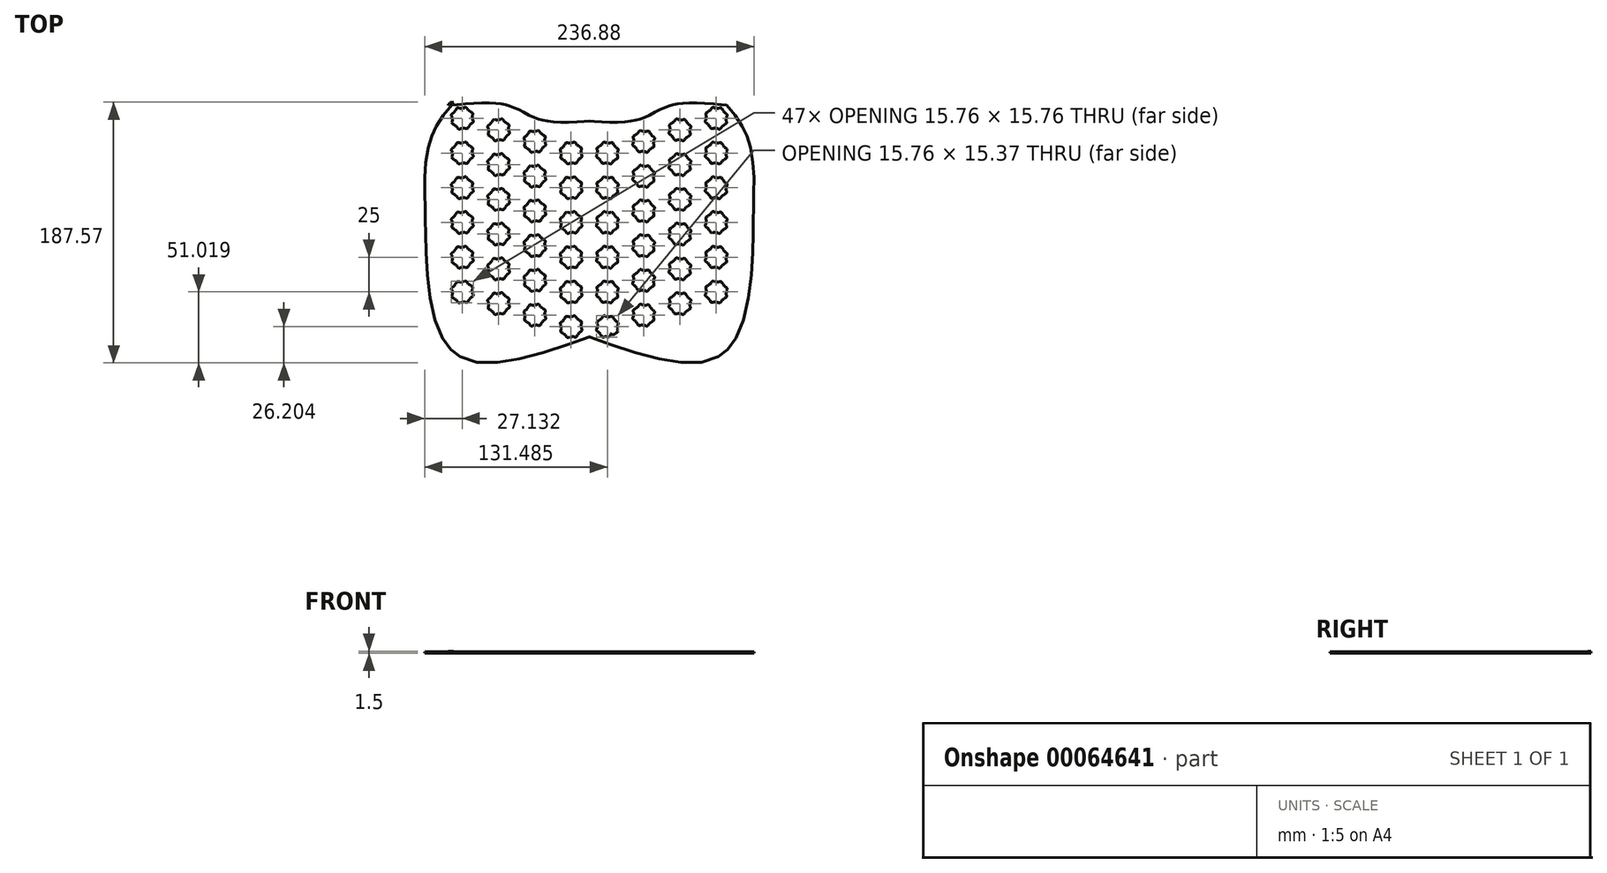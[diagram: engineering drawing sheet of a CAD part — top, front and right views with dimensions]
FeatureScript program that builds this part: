
annotation { "Feature Type Name" : "Feature", "Feature Type Description" : "" }
export const myFeature = defineFeature(function(context is Context, id is Id, definition is map)
    precondition{}
    {
        {
            var Q0;
            Q0=qCreatedBy(makeId("Top.planeOp"),FACE);
            var sketch = newSketch(context, id + "F0", { "sketchPlane" : qUnion([Q0])});
            skLineSegment(sketch, "E0", {"start": v(-116.5, 0) * mm, "end": v(139.03, 0) * mm, "construction": true});
            skLineSegment(sketch, "E1.0", {"start": v(-116.5, -90) * mm, "end": v(139.03, -90) * mm, "construction": true});
            skLineSegment(sketch, "E2.0", {"start": v(-116.5, 90) * mm, "end": v(139.03, 90) * mm, "construction": true});
            skLineSegment(sketch, "E3", {"start": v(0, 90) * mm, "end": v(0, -92.69) * mm, "construction": true});
            skLineSegment(sketch, "E4.0", {"start": v(-100, 90) * mm, "end": v(-100, -92.69) * mm, "construction": true});
            skLineSegment(sketch, "E5.0", {"start": v(-120, 90) * mm, "end": v(-120, -92.69) * mm, "construction": true});
            skLineSegment(sketch, "E6.0", {"start": v(120, 90) * mm, "end": v(120, -92.69) * mm, "construction": true});
            skLineSegment(sketch, "E7.0", {"start": v(100, 90) * mm, "end": v(100, -92.69) * mm, "construction": true});
            skFitSpline(sketch, "E8", {"points": [v(-100, 90) * mm, v(-114.02, 69.47) * mm, v(-120, 43.4) * mm, v(-120, 8.31) * mm, v(-100, -90) * mm, v(0, -80.79) * mm], "startDerivative": vector(-114.58, -138.92) * mm, "endDerivative": vector(433.2, 151.03) * mm});
            skFitSpline(sketch, "E9", {"points": [v(0, 78.79) * mm, v(-34.86, 79.72) * mm, v(-58.45, 90) * mm, v(-100, 90) * mm], "startDerivative": vector(-110.99, -8.68) * mm, "endDerivative": vector(-123.02, -12.63) * mm});
            skArc(sketch, "E10.filletArc", {"start": v(-97.54, 90.25) * mm, "mid": v(-99.77, 89.57) * mm, "end": v(-101.57, 88.09) * mm});
            skFitSpline(sketch, "E11.MirrorCS", {"points": [v(0, 78.79) * mm, v(34.86, 79.72) * mm, v(58.45, 90) * mm, v(100, 90) * mm], "startDerivative": vector(110.99, -8.68) * mm, "endDerivative": vector(123.02, -12.63) * mm});
            skFitSpline(sketch, "E12.MirrorCS", {"points": [v(100, 90) * mm, v(114.02, 69.47) * mm, v(120, 43.4) * mm, v(120, 8.31) * mm, v(100, -90) * mm, v(0, -80.79) * mm], "startDerivative": vector(114.58, -138.92) * mm, "endDerivative": vector(-433.2, 151.03) * mm});
            skArc(sketch, "E13.MirrorCS", {"start": v(97.54, 90.25) * mm, "mid": v(99.77, 89.57) * mm, "end": v(101.57, 88.09) * mm});
            skFitSpline(sketch, "E14.0", {"points": [v(0.16, 76.8) * mm, v(-2.16, 76.61) * mm, v(-6.8, 76.25) * mm, v(-13.69, 75.85) * mm, v(-20.42, 75.74) * mm, v(-25.82, 76.02) * mm, v(-29.97, 76.55) * mm, v(-32.48, 77.03) * mm, v(-34.44, 77.51) * mm, v(-36.35, 78.06) * mm, v(-38.65, 78.88) * mm, v(-41.26, 80) * mm, v(-44.61, 81.61) * mm, v(-47.82, 83.32) * mm, v(-51.02, 84.95) * mm, v(-53.45, 86.09) * mm, v(-55.94, 87.11) * mm, v(-58.1, 87.84) * mm, v(-59.9, 88.32) * mm, v(-61.76, 88.75) * mm, v(-64.2, 89.18) * mm, v(-67.3, 89.53) * mm, v(-71.61, 89.8) * mm, v(-77.33, 89.83) * mm, v(-84.6, 89.45) * mm, v(-92.12, 88.8) * mm, v(-97.23, 88.27) * mm, v(-99.8, 88.01) * mm]});
            skFitSpline(sketch, "E15.0", {"points": [v(-0.16, 76.8) * mm, v(2.16, 76.61) * mm, v(6.8, 76.25) * mm, v(13.69, 75.85) * mm, v(20.42, 75.74) * mm, v(25.82, 76.02) * mm, v(29.97, 76.55) * mm, v(32.48, 77.03) * mm, v(34.44, 77.51) * mm, v(36.35, 78.06) * mm, v(38.65, 78.88) * mm, v(41.26, 80) * mm, v(44.61, 81.61) * mm, v(47.82, 83.32) * mm, v(51.02, 84.95) * mm, v(53.45, 86.09) * mm, v(55.94, 87.11) * mm, v(58.1, 87.84) * mm, v(59.9, 88.32) * mm, v(61.76, 88.75) * mm, v(64.2, 89.18) * mm, v(67.3, 89.53) * mm, v(71.61, 89.8) * mm, v(77.33, 89.83) * mm, v(84.6, 89.45) * mm, v(92.12, 88.8) * mm, v(97.23, 88.27) * mm, v(99.8, 88.01) * mm]});
            skFitSpline(sketch, "E16.0", {"points": [v(98.46, 88.73) * mm, v(99.65, 87.28) * mm, v(102.03, 84.4) * mm, v(105.43, 80.03) * mm, v(108.04, 76.27) * mm, v(109.92, 73.15) * mm, v(111.23, 70.74) * mm, v(112.4, 68.25) * mm, v(113.46, 65.66) * mm, v(114.39, 62.97) * mm, v(115.47, 59.3) * mm, v(116.56, 54.56) * mm, v(117.47, 48.83) * mm, v(118.05, 43.2) * mm, v(118.35, 37.81) * mm, v(118.44, 32.29) * mm, v(118.37, 26.22) * mm, v(118.24, 20.4) * mm, v(118.12, 15.08) * mm, v(118.05, 11.45) * mm, v(118, 8.34) * mm, v(117.95, 5.08) * mm, v(117.9, 0.76) * mm, v(117.8, -4.78) * mm, v(117.63, -12.53) * mm, v(117.26, -22.79) * mm, v(116.37, -35.51) * mm, v(114.87, -48.17) * mm, v(112.6, -60.27) * mm, v(109.38, -71.31) * mm, v(105.8, -79.21) * mm, v(102.33, -84.5) * mm, v(99.92, -87.34) * mm, v(97.83, -89.3) * mm, v(95.62, -91.08) * mm, v(91.46, -93.7) * mm, v(84.64, -96.16) * mm, v(75.12, -97.29) * mm, v(64.45, -96.8) * mm, v(52.83, -94.9) * mm, v(40.45, -91.9) * mm, v(23.2, -86.76) * mm, v(9.68, -82.05) * mm, v(0.66, -78.9) * mm]});
            skFitSpline(sketch, "E17.0", {"points": [v(-98.46, 88.73) * mm, v(-99.65, 87.28) * mm, v(-102.03, 84.4) * mm, v(-105.43, 80.03) * mm, v(-108.04, 76.27) * mm, v(-109.92, 73.15) * mm, v(-111.23, 70.74) * mm, v(-112.4, 68.25) * mm, v(-113.46, 65.66) * mm, v(-114.39, 62.97) * mm, v(-115.47, 59.3) * mm, v(-116.56, 54.56) * mm, v(-117.47, 48.83) * mm, v(-118.05, 43.2) * mm, v(-118.35, 37.81) * mm, v(-118.44, 32.29) * mm, v(-118.37, 26.22) * mm, v(-118.24, 20.4) * mm, v(-118.12, 15.08) * mm, v(-118.05, 11.45) * mm, v(-118, 8.34) * mm, v(-117.95, 5.08) * mm, v(-117.9, 0.76) * mm, v(-117.8, -4.78) * mm, v(-117.63, -12.53) * mm, v(-117.26, -22.79) * mm, v(-116.37, -35.51) * mm, v(-114.87, -48.17) * mm, v(-112.6, -60.27) * mm, v(-109.38, -71.31) * mm, v(-105.8, -79.21) * mm, v(-102.33, -84.5) * mm, v(-99.92, -87.34) * mm, v(-97.83, -89.3) * mm, v(-95.62, -91.08) * mm, v(-91.46, -93.7) * mm, v(-84.64, -96.16) * mm, v(-75.12, -97.29) * mm, v(-64.45, -96.8) * mm, v(-52.83, -94.9) * mm, v(-40.45, -91.9) * mm, v(-23.2, -86.76) * mm, v(-9.68, -82.05) * mm, v(-0.66, -78.9) * mm]});
            skFitSpline(sketch, "E18", {"points": [v(-0.66, -78.9) * mm, v(0, -78.63) * mm, v(0.66, -78.9) * mm], "startDerivative": vector(1.32, 0.81) * mm, "endDerivative": vector(1.32, -0.81) * mm});
            skArc(sketch, "E19.filletArc", {"start": v(100.56, 86.17) * mm, "mid": v(98.75, 87.66) * mm, "end": v(96.52, 88.35) * mm});
            skArc(sketch, "E20.filletArc", {"start": v(-96.52, 88.35) * mm, "mid": v(-98.75, 87.66) * mm, "end": v(-100.56, 86.17) * mm});
            skCircle(sketch, "E21", {"center": v(-91.3, 78.7) * mm, "radius": 5.5 * mm});
            skCircle(sketch, "E22", {"center": v(-85.82, 78.4) * mm, "radius": 2.01 * mm});
            skEllipse(sketch, "E23", {"center": v(-86.08, 80.4) * mm, "majorRadius": 3.02 * mm, "minorRadius": 1.73 * mm, "majorAxis": v(0.58, 0.81)});
            skEllipse(sketch, "E24.1.0", {"center": v(-88.81, 83.6) * mm, "majorRadius": 3.02 * mm, "minorRadius": 1.73 * mm, "majorAxis": v(-0.16, 0.99)});
            skCircle(sketch, "E24.1.1", {"center": v(-87.22, 82.38) * mm, "radius": 2.01 * mm});
            skEllipse(sketch, "E24.2.0", {"center": v(-93.01, 83.93) * mm, "majorRadius": 3.02 * mm, "minorRadius": 1.73 * mm, "majorAxis": v(-0.81, 0.58)});
            skCircle(sketch, "E24.2.1", {"center": v(-91.02, 84.2) * mm, "radius": 2.01 * mm});
            skEllipse(sketch, "E24.3.0", {"center": v(-96.2, 81.2) * mm, "majorRadius": 3.02 * mm, "minorRadius": 1.73 * mm, "majorAxis": v(-0.99, -0.16)});
            skCircle(sketch, "E24.3.1", {"center": v(-94.99, 82.79) * mm, "radius": 2.01 * mm});
            skEllipse(sketch, "E24.4.0", {"center": v(-96.54, 77) * mm, "majorRadius": 3.02 * mm, "minorRadius": 1.73 * mm, "majorAxis": v(-0.58, -0.81)});
            skCircle(sketch, "E24.4.1", {"center": v(-96.8, 78.99) * mm, "radius": 2.01 * mm});
            skEllipse(sketch, "E24.5.0", {"center": v(-93.8, 73.8) * mm, "majorRadius": 3.02 * mm, "minorRadius": 1.73 * mm, "majorAxis": v(0.16, -0.99)});
            skCircle(sketch, "E24.5.1", {"center": v(-95.4, 75.02) * mm, "radius": 2.01 * mm});
            skEllipse(sketch, "E24.6.0", {"center": v(-89.6, 73.47) * mm, "majorRadius": 3.02 * mm, "minorRadius": 1.73 * mm, "majorAxis": v(0.81, -0.58)});
            skCircle(sketch, "E24.6.1", {"center": v(-91.6, 73.2) * mm, "radius": 2.01 * mm});
            skEllipse(sketch, "E24.7.0", {"center": v(-86.4, 76.2) * mm, "majorRadius": 3.02 * mm, "minorRadius": 1.73 * mm, "majorAxis": v(0.99, 0.16)});
            skCircle(sketch, "E24.7.1", {"center": v(-87.63, 74.6) * mm, "radius": 2.01 * mm});
            skEllipse(sketch, "E25.0.1.0", {"center": v(-93.01, 58.93) * mm, "majorRadius": 3.02 * mm, "minorRadius": 1.73 * mm, "majorAxis": v(-0.81, 0.58)});
            skCircle(sketch, "E25.0.1.1", {"center": v(-91.6, 48.2) * mm, "radius": 2.01 * mm});
            skCircle(sketch, "E25.0.1.2", {"center": v(-91.02, 59.2) * mm, "radius": 2.01 * mm});
            skCircle(sketch, "E25.0.1.3", {"center": v(-94.99, 57.79) * mm, "radius": 2.01 * mm});
            skEllipse(sketch, "E25.0.1.4", {"center": v(-86.4, 51.2) * mm, "majorRadius": 3.02 * mm, "minorRadius": 1.73 * mm, "majorAxis": v(0.99, 0.16)});
            skEllipse(sketch, "E25.0.1.5", {"center": v(-96.2, 56.2) * mm, "majorRadius": 3.02 * mm, "minorRadius": 1.73 * mm, "majorAxis": v(-0.99, -0.16)});
            skCircle(sketch, "E25.0.1.6", {"center": v(-87.63, 49.6) * mm, "radius": 2.01 * mm});
            skEllipse(sketch, "E25.0.1.7", {"center": v(-96.54, 52) * mm, "majorRadius": 3.02 * mm, "minorRadius": 1.73 * mm, "majorAxis": v(-0.58, -0.81)});
            skCircle(sketch, "E25.0.1.8", {"center": v(-85.82, 53.4) * mm, "radius": 2.01 * mm});
            skCircle(sketch, "E25.0.1.9", {"center": v(-96.8, 53.99) * mm, "radius": 2.01 * mm});
            skEllipse(sketch, "E25.0.1.10", {"center": v(-86.08, 55.4) * mm, "majorRadius": 3.02 * mm, "minorRadius": 1.73 * mm, "majorAxis": v(0.58, 0.81)});
            skEllipse(sketch, "E25.0.1.11", {"center": v(-93.8, 48.8) * mm, "majorRadius": 3.02 * mm, "minorRadius": 1.73 * mm, "majorAxis": v(0.16, -0.99)});
            skPoint(sketch, "E25.0.1.12", {"position": v(-91.3, 53.7) * mm});
            skEllipse(sketch, "E25.0.1.13", {"center": v(-88.81, 58.6) * mm, "majorRadius": 3.02 * mm, "minorRadius": 1.73 * mm, "majorAxis": v(-0.16, 0.99)});
            skCircle(sketch, "E25.0.1.14", {"center": v(-95.4, 50.02) * mm, "radius": 2.01 * mm});
            skCircle(sketch, "E25.0.1.15", {"center": v(-87.22, 57.38) * mm, "radius": 2.01 * mm});
            skEllipse(sketch, "E25.0.1.16", {"center": v(-89.6, 48.47) * mm, "majorRadius": 3.02 * mm, "minorRadius": 1.73 * mm, "majorAxis": v(0.81, -0.58)});
            skCircle(sketch, "E25.0.1.17", {"center": v(-91.3, 53.7) * mm, "radius": 5.5 * mm});
            skEllipse(sketch, "E25.0.2.0", {"center": v(-93.01, 33.93) * mm, "majorRadius": 3.02 * mm, "minorRadius": 1.73 * mm, "majorAxis": v(-0.81, 0.58)});
            skCircle(sketch, "E25.0.2.1", {"center": v(-91.6, 23.2) * mm, "radius": 2.01 * mm});
            skCircle(sketch, "E25.0.2.2", {"center": v(-91.02, 34.2) * mm, "radius": 2.01 * mm});
            skCircle(sketch, "E25.0.2.3", {"center": v(-94.99, 32.79) * mm, "radius": 2.01 * mm});
            skEllipse(sketch, "E25.0.2.4", {"center": v(-86.4, 26.2) * mm, "majorRadius": 3.02 * mm, "minorRadius": 1.73 * mm, "majorAxis": v(0.99, 0.16)});
            skEllipse(sketch, "E25.0.2.5", {"center": v(-96.2, 31.2) * mm, "majorRadius": 3.02 * mm, "minorRadius": 1.73 * mm, "majorAxis": v(-0.99, -0.16)});
            skCircle(sketch, "E25.0.2.6", {"center": v(-87.63, 24.6) * mm, "radius": 2.01 * mm});
            skEllipse(sketch, "E25.0.2.7", {"center": v(-96.54, 27) * mm, "majorRadius": 3.02 * mm, "minorRadius": 1.73 * mm, "majorAxis": v(-0.58, -0.81)});
            skCircle(sketch, "E25.0.2.8", {"center": v(-85.82, 28.4) * mm, "radius": 2.01 * mm});
            skCircle(sketch, "E25.0.2.9", {"center": v(-96.8, 28.99) * mm, "radius": 2.01 * mm});
            skEllipse(sketch, "E25.0.2.10", {"center": v(-86.08, 30.4) * mm, "majorRadius": 3.02 * mm, "minorRadius": 1.73 * mm, "majorAxis": v(0.58, 0.81)});
            skEllipse(sketch, "E25.0.2.11", {"center": v(-93.8, 23.8) * mm, "majorRadius": 3.02 * mm, "minorRadius": 1.73 * mm, "majorAxis": v(0.16, -0.99)});
            skPoint(sketch, "E25.0.2.12", {"position": v(-91.3, 28.7) * mm});
            skEllipse(sketch, "E25.0.2.13", {"center": v(-88.81, 33.6) * mm, "majorRadius": 3.02 * mm, "minorRadius": 1.73 * mm, "majorAxis": v(-0.16, 0.99)});
            skCircle(sketch, "E25.0.2.14", {"center": v(-95.4, 25.02) * mm, "radius": 2.01 * mm});
            skCircle(sketch, "E25.0.2.15", {"center": v(-87.22, 32.38) * mm, "radius": 2.01 * mm});
            skEllipse(sketch, "E25.0.2.16", {"center": v(-89.6, 23.47) * mm, "majorRadius": 3.02 * mm, "minorRadius": 1.73 * mm, "majorAxis": v(0.81, -0.58)});
            skCircle(sketch, "E25.0.2.17", {"center": v(-91.3, 28.7) * mm, "radius": 5.5 * mm});
            skEllipse(sketch, "E25.0.3.0", {"center": v(-93.01, 8.93) * mm, "majorRadius": 3.02 * mm, "minorRadius": 1.73 * mm, "majorAxis": v(-0.81, 0.58)});
            skCircle(sketch, "E25.0.3.1", {"center": v(-91.6, -1.8) * mm, "radius": 2.01 * mm});
            skCircle(sketch, "E25.0.3.2", {"center": v(-91.02, 9.2) * mm, "radius": 2.01 * mm});
            skCircle(sketch, "E25.0.3.3", {"center": v(-94.99, 7.79) * mm, "radius": 2.01 * mm});
            skEllipse(sketch, "E25.0.3.4", {"center": v(-86.4, 1.2) * mm, "majorRadius": 3.02 * mm, "minorRadius": 1.73 * mm, "majorAxis": v(0.99, 0.16)});
            skEllipse(sketch, "E25.0.3.5", {"center": v(-96.2, 6.2) * mm, "majorRadius": 3.02 * mm, "minorRadius": 1.73 * mm, "majorAxis": v(-0.99, -0.16)});
            skCircle(sketch, "E25.0.3.6", {"center": v(-87.63, -0.4) * mm, "radius": 2.01 * mm});
            skEllipse(sketch, "E25.0.3.7", {"center": v(-96.54, 2) * mm, "majorRadius": 3.02 * mm, "minorRadius": 1.73 * mm, "majorAxis": v(-0.58, -0.81)});
            skCircle(sketch, "E25.0.3.8", {"center": v(-85.82, 3.4) * mm, "radius": 2.01 * mm});
            skCircle(sketch, "E25.0.3.9", {"center": v(-96.8, 3.99) * mm, "radius": 2.01 * mm});
            skEllipse(sketch, "E25.0.3.10", {"center": v(-86.08, 5.4) * mm, "majorRadius": 3.02 * mm, "minorRadius": 1.73 * mm, "majorAxis": v(0.58, 0.81)});
            skEllipse(sketch, "E25.0.3.11", {"center": v(-93.8, -1.2) * mm, "majorRadius": 3.02 * mm, "minorRadius": 1.73 * mm, "majorAxis": v(0.16, -0.99)});
            skPoint(sketch, "E25.0.3.12", {"position": v(-91.3, 3.7) * mm});
            skEllipse(sketch, "E25.0.3.13", {"center": v(-88.81, 8.6) * mm, "majorRadius": 3.02 * mm, "minorRadius": 1.73 * mm, "majorAxis": v(-0.16, 0.99)});
            skCircle(sketch, "E25.0.3.14", {"center": v(-95.4, 0.02) * mm, "radius": 2.01 * mm});
            skCircle(sketch, "E25.0.3.15", {"center": v(-87.22, 7.38) * mm, "radius": 2.01 * mm});
            skEllipse(sketch, "E25.0.3.16", {"center": v(-89.6, -1.53) * mm, "majorRadius": 3.02 * mm, "minorRadius": 1.73 * mm, "majorAxis": v(0.81, -0.58)});
            skCircle(sketch, "E25.0.3.17", {"center": v(-91.3, 3.7) * mm, "radius": 5.5 * mm});
            skEllipse(sketch, "E25.0.4.0", {"center": v(-93.01, -16.07) * mm, "majorRadius": 3.02 * mm, "minorRadius": 1.73 * mm, "majorAxis": v(-0.81, 0.58)});
            skCircle(sketch, "E25.0.4.1", {"center": v(-91.6, -26.8) * mm, "radius": 2.01 * mm});
            skCircle(sketch, "E25.0.4.2", {"center": v(-91.02, -15.8) * mm, "radius": 2.01 * mm});
            skCircle(sketch, "E25.0.4.3", {"center": v(-94.99, -17.21) * mm, "radius": 2.01 * mm});
            skEllipse(sketch, "E25.0.4.4", {"center": v(-86.4, -23.8) * mm, "majorRadius": 3.02 * mm, "minorRadius": 1.73 * mm, "majorAxis": v(0.99, 0.16)});
            skEllipse(sketch, "E25.0.4.5", {"center": v(-96.2, -18.8) * mm, "majorRadius": 3.02 * mm, "minorRadius": 1.73 * mm, "majorAxis": v(-0.99, -0.16)});
            skCircle(sketch, "E25.0.4.6", {"center": v(-87.63, -25.4) * mm, "radius": 2.01 * mm});
            skEllipse(sketch, "E25.0.4.7", {"center": v(-96.54, -23) * mm, "majorRadius": 3.02 * mm, "minorRadius": 1.73 * mm, "majorAxis": v(-0.58, -0.81)});
            skCircle(sketch, "E25.0.4.8", {"center": v(-85.82, -21.6) * mm, "radius": 2.01 * mm});
            skCircle(sketch, "E25.0.4.9", {"center": v(-96.8, -21.01) * mm, "radius": 2.01 * mm});
            skEllipse(sketch, "E25.0.4.10", {"center": v(-86.08, -19.6) * mm, "majorRadius": 3.02 * mm, "minorRadius": 1.73 * mm, "majorAxis": v(0.58, 0.81)});
            skEllipse(sketch, "E25.0.4.11", {"center": v(-93.8, -26.2) * mm, "majorRadius": 3.02 * mm, "minorRadius": 1.73 * mm, "majorAxis": v(0.16, -0.99)});
            skPoint(sketch, "E25.0.4.12", {"position": v(-91.3, -21.3) * mm});
            skEllipse(sketch, "E25.0.4.13", {"center": v(-88.81, -16.4) * mm, "majorRadius": 3.02 * mm, "minorRadius": 1.73 * mm, "majorAxis": v(-0.16, 0.99)});
            skCircle(sketch, "E25.0.4.14", {"center": v(-95.4, -24.98) * mm, "radius": 2.01 * mm});
            skCircle(sketch, "E25.0.4.15", {"center": v(-87.22, -17.62) * mm, "radius": 2.01 * mm});
            skEllipse(sketch, "E25.0.4.16", {"center": v(-89.6, -26.53) * mm, "majorRadius": 3.02 * mm, "minorRadius": 1.73 * mm, "majorAxis": v(0.81, -0.58)});
            skCircle(sketch, "E25.0.4.17", {"center": v(-91.3, -21.3) * mm, "radius": 5.5 * mm});
            skEllipse(sketch, "E25.0.5.0", {"center": v(-93.01, -41.07) * mm, "majorRadius": 3.02 * mm, "minorRadius": 1.73 * mm, "majorAxis": v(-0.81, 0.58)});
            skCircle(sketch, "E25.0.5.1", {"center": v(-91.6, -51.8) * mm, "radius": 2.01 * mm});
            skCircle(sketch, "E25.0.5.2", {"center": v(-91.02, -40.8) * mm, "radius": 2.01 * mm});
            skCircle(sketch, "E25.0.5.3", {"center": v(-94.99, -42.21) * mm, "radius": 2.01 * mm});
            skEllipse(sketch, "E25.0.5.4", {"center": v(-86.4, -48.8) * mm, "majorRadius": 3.02 * mm, "minorRadius": 1.73 * mm, "majorAxis": v(0.99, 0.16)});
            skEllipse(sketch, "E25.0.5.5", {"center": v(-96.2, -43.8) * mm, "majorRadius": 3.02 * mm, "minorRadius": 1.73 * mm, "majorAxis": v(-0.99, -0.16)});
            skCircle(sketch, "E25.0.5.6", {"center": v(-87.63, -50.4) * mm, "radius": 2.01 * mm});
            skEllipse(sketch, "E25.0.5.7", {"center": v(-96.54, -48) * mm, "majorRadius": 3.02 * mm, "minorRadius": 1.73 * mm, "majorAxis": v(-0.58, -0.81)});
            skCircle(sketch, "E25.0.5.8", {"center": v(-85.82, -46.6) * mm, "radius": 2.01 * mm});
            skCircle(sketch, "E25.0.5.9", {"center": v(-96.8, -46.01) * mm, "radius": 2.01 * mm});
            skEllipse(sketch, "E25.0.5.10", {"center": v(-86.08, -44.6) * mm, "majorRadius": 3.02 * mm, "minorRadius": 1.73 * mm, "majorAxis": v(0.58, 0.81)});
            skEllipse(sketch, "E25.0.5.11", {"center": v(-93.8, -51.2) * mm, "majorRadius": 3.02 * mm, "minorRadius": 1.73 * mm, "majorAxis": v(0.16, -0.99)});
            skPoint(sketch, "E25.0.5.12", {"position": v(-91.3, -46.3) * mm});
            skEllipse(sketch, "E25.0.5.13", {"center": v(-88.81, -41.4) * mm, "majorRadius": 3.02 * mm, "minorRadius": 1.73 * mm, "majorAxis": v(-0.16, 0.99)});
            skCircle(sketch, "E25.0.5.14", {"center": v(-95.4, -49.98) * mm, "radius": 2.01 * mm});
            skCircle(sketch, "E25.0.5.15", {"center": v(-87.22, -42.62) * mm, "radius": 2.01 * mm});
            skEllipse(sketch, "E25.0.5.16", {"center": v(-89.6, -51.53) * mm, "majorRadius": 3.02 * mm, "minorRadius": 1.73 * mm, "majorAxis": v(0.81, -0.58)});
            skCircle(sketch, "E25.0.5.17", {"center": v(-91.3, -46.3) * mm, "radius": 5.5 * mm});
            skEllipse(sketch, "E25.1.0.0", {"center": v(-66.92, 75.6) * mm, "majorRadius": 3.02 * mm, "minorRadius": 1.73 * mm, "majorAxis": v(-0.81, 0.58)});
            skCircle(sketch, "E25.1.0.1", {"center": v(-65.51, 64.87) * mm, "radius": 2.01 * mm});
            skCircle(sketch, "E25.1.0.2", {"center": v(-64.93, 75.85) * mm, "radius": 2.01 * mm});
            skCircle(sketch, "E25.1.0.3", {"center": v(-68.9, 74.45) * mm, "radius": 2.01 * mm});
            skEllipse(sketch, "E25.1.0.4", {"center": v(-60.32, 67.87) * mm, "majorRadius": 3.02 * mm, "minorRadius": 1.73 * mm, "majorAxis": v(0.99, 0.16)});
            skEllipse(sketch, "E25.1.0.5", {"center": v(-70.12, 72.85) * mm, "majorRadius": 3.02 * mm, "minorRadius": 1.73 * mm, "majorAxis": v(-0.99, -0.16)});
            skCircle(sketch, "E25.1.0.6", {"center": v(-61.54, 66.27) * mm, "radius": 2.01 * mm});
            skEllipse(sketch, "E25.1.0.7", {"center": v(-70.45, 68.66) * mm, "majorRadius": 3.02 * mm, "minorRadius": 1.73 * mm, "majorAxis": v(-0.58, -0.81)});
            skCircle(sketch, "E25.1.0.8", {"center": v(-59.73, 70.07) * mm, "radius": 2.01 * mm});
            skCircle(sketch, "E25.1.0.9", {"center": v(-70.71, 70.65) * mm, "radius": 2.01 * mm});
            skEllipse(sketch, "E25.1.0.10", {"center": v(-60, 72.06) * mm, "majorRadius": 3.02 * mm, "minorRadius": 1.73 * mm, "majorAxis": v(0.58, 0.81)});
            skEllipse(sketch, "E25.1.0.11", {"center": v(-67.71, 65.46) * mm, "majorRadius": 3.02 * mm, "minorRadius": 1.73 * mm, "majorAxis": v(0.16, -0.99)});
            skPoint(sketch, "E25.1.0.12", {"position": v(-65.22, 70.36) * mm});
            skEllipse(sketch, "E25.1.0.13", {"center": v(-62.73, 75.26) * mm, "majorRadius": 3.02 * mm, "minorRadius": 1.73 * mm, "majorAxis": v(-0.16, 0.99)});
            skCircle(sketch, "E25.1.0.14", {"center": v(-69.3, 66.68) * mm, "radius": 2.01 * mm});
            skCircle(sketch, "E25.1.0.15", {"center": v(-61.13, 74.04) * mm, "radius": 2.01 * mm});
            skEllipse(sketch, "E25.1.0.16", {"center": v(-63.52, 65.13) * mm, "majorRadius": 3.02 * mm, "minorRadius": 1.73 * mm, "majorAxis": v(0.81, -0.58)});
            skCircle(sketch, "E25.1.0.17", {"center": v(-65.22, 70.36) * mm, "radius": 5.5 * mm});
            skEllipse(sketch, "E25.1.1.0", {"center": v(-66.92, 50.6) * mm, "majorRadius": 3.02 * mm, "minorRadius": 1.73 * mm, "majorAxis": v(-0.81, 0.58)});
            skCircle(sketch, "E25.1.1.1", {"center": v(-65.51, 39.87) * mm, "radius": 2.01 * mm});
            skCircle(sketch, "E25.1.1.2", {"center": v(-64.93, 50.85) * mm, "radius": 2.01 * mm});
            skCircle(sketch, "E25.1.1.3", {"center": v(-68.9, 49.45) * mm, "radius": 2.01 * mm});
            skEllipse(sketch, "E25.1.1.4", {"center": v(-60.32, 42.87) * mm, "majorRadius": 3.02 * mm, "minorRadius": 1.73 * mm, "majorAxis": v(0.99, 0.16)});
            skEllipse(sketch, "E25.1.1.5", {"center": v(-70.12, 47.85) * mm, "majorRadius": 3.02 * mm, "minorRadius": 1.73 * mm, "majorAxis": v(-0.99, -0.16)});
            skCircle(sketch, "E25.1.1.6", {"center": v(-61.54, 41.27) * mm, "radius": 2.01 * mm});
            skEllipse(sketch, "E25.1.1.7", {"center": v(-70.45, 43.66) * mm, "majorRadius": 3.02 * mm, "minorRadius": 1.73 * mm, "majorAxis": v(-0.58, -0.81)});
            skCircle(sketch, "E25.1.1.8", {"center": v(-59.73, 45.07) * mm, "radius": 2.01 * mm});
            skCircle(sketch, "E25.1.1.9", {"center": v(-70.71, 45.65) * mm, "radius": 2.01 * mm});
            skEllipse(sketch, "E25.1.1.10", {"center": v(-60, 47.06) * mm, "majorRadius": 3.02 * mm, "minorRadius": 1.73 * mm, "majorAxis": v(0.58, 0.81)});
            skEllipse(sketch, "E25.1.1.11", {"center": v(-67.71, 40.46) * mm, "majorRadius": 3.02 * mm, "minorRadius": 1.73 * mm, "majorAxis": v(0.16, -0.99)});
            skPoint(sketch, "E25.1.1.12", {"position": v(-65.22, 45.36) * mm});
            skEllipse(sketch, "E25.1.1.13", {"center": v(-62.73, 50.26) * mm, "majorRadius": 3.02 * mm, "minorRadius": 1.73 * mm, "majorAxis": v(-0.16, 0.99)});
            skCircle(sketch, "E25.1.1.14", {"center": v(-69.3, 41.68) * mm, "radius": 2.01 * mm});
            skCircle(sketch, "E25.1.1.15", {"center": v(-61.13, 49.04) * mm, "radius": 2.01 * mm});
            skEllipse(sketch, "E25.1.1.16", {"center": v(-63.52, 40.13) * mm, "majorRadius": 3.02 * mm, "minorRadius": 1.73 * mm, "majorAxis": v(0.81, -0.58)});
            skCircle(sketch, "E25.1.1.17", {"center": v(-65.22, 45.36) * mm, "radius": 5.5 * mm});
            skEllipse(sketch, "E25.1.2.0", {"center": v(-66.92, 25.6) * mm, "majorRadius": 3.02 * mm, "minorRadius": 1.73 * mm, "majorAxis": v(-0.81, 0.58)});
            skCircle(sketch, "E25.1.2.1", {"center": v(-65.51, 14.87) * mm, "radius": 2.01 * mm});
            skCircle(sketch, "E25.1.2.2", {"center": v(-64.93, 25.85) * mm, "radius": 2.01 * mm});
            skCircle(sketch, "E25.1.2.3", {"center": v(-68.9, 24.45) * mm, "radius": 2.01 * mm});
            skEllipse(sketch, "E25.1.2.4", {"center": v(-60.32, 17.87) * mm, "majorRadius": 3.02 * mm, "minorRadius": 1.73 * mm, "majorAxis": v(0.99, 0.16)});
            skEllipse(sketch, "E25.1.2.5", {"center": v(-70.12, 22.85) * mm, "majorRadius": 3.02 * mm, "minorRadius": 1.73 * mm, "majorAxis": v(-0.99, -0.16)});
            skCircle(sketch, "E25.1.2.6", {"center": v(-61.54, 16.27) * mm, "radius": 2.01 * mm});
            skEllipse(sketch, "E25.1.2.7", {"center": v(-70.45, 18.66) * mm, "majorRadius": 3.02 * mm, "minorRadius": 1.73 * mm, "majorAxis": v(-0.58, -0.81)});
            skCircle(sketch, "E25.1.2.8", {"center": v(-59.73, 20.07) * mm, "radius": 2.01 * mm});
            skCircle(sketch, "E25.1.2.9", {"center": v(-70.71, 20.65) * mm, "radius": 2.01 * mm});
            skEllipse(sketch, "E25.1.2.10", {"center": v(-60, 22.06) * mm, "majorRadius": 3.02 * mm, "minorRadius": 1.73 * mm, "majorAxis": v(0.58, 0.81)});
            skEllipse(sketch, "E25.1.2.11", {"center": v(-67.71, 15.46) * mm, "majorRadius": 3.02 * mm, "minorRadius": 1.73 * mm, "majorAxis": v(0.16, -0.99)});
            skPoint(sketch, "E25.1.2.12", {"position": v(-65.22, 20.36) * mm});
            skEllipse(sketch, "E25.1.2.13", {"center": v(-62.73, 25.26) * mm, "majorRadius": 3.02 * mm, "minorRadius": 1.73 * mm, "majorAxis": v(-0.16, 0.99)});
            skCircle(sketch, "E25.1.2.14", {"center": v(-69.3, 16.68) * mm, "radius": 2.01 * mm});
            skCircle(sketch, "E25.1.2.15", {"center": v(-61.13, 24.04) * mm, "radius": 2.01 * mm});
            skEllipse(sketch, "E25.1.2.16", {"center": v(-63.52, 15.13) * mm, "majorRadius": 3.02 * mm, "minorRadius": 1.73 * mm, "majorAxis": v(0.81, -0.58)});
            skCircle(sketch, "E25.1.2.17", {"center": v(-65.22, 20.36) * mm, "radius": 5.5 * mm});
            skEllipse(sketch, "E25.1.3.0", {"center": v(-66.92, 0.6) * mm, "majorRadius": 3.02 * mm, "minorRadius": 1.73 * mm, "majorAxis": v(-0.81, 0.58)});
            skCircle(sketch, "E25.1.3.1", {"center": v(-65.51, -10.13) * mm, "radius": 2.01 * mm});
            skCircle(sketch, "E25.1.3.2", {"center": v(-64.93, 0.85) * mm, "radius": 2.01 * mm});
            skCircle(sketch, "E25.1.3.3", {"center": v(-68.9, -0.55) * mm, "radius": 2.01 * mm});
            skEllipse(sketch, "E25.1.3.4", {"center": v(-60.32, -7.13) * mm, "majorRadius": 3.02 * mm, "minorRadius": 1.73 * mm, "majorAxis": v(0.99, 0.16)});
            skEllipse(sketch, "E25.1.3.5", {"center": v(-70.12, -2.15) * mm, "majorRadius": 3.02 * mm, "minorRadius": 1.73 * mm, "majorAxis": v(-0.99, -0.16)});
            skCircle(sketch, "E25.1.3.6", {"center": v(-61.54, -8.73) * mm, "radius": 2.01 * mm});
            skEllipse(sketch, "E25.1.3.7", {"center": v(-70.45, -6.34) * mm, "majorRadius": 3.02 * mm, "minorRadius": 1.73 * mm, "majorAxis": v(-0.58, -0.81)});
            skCircle(sketch, "E25.1.3.8", {"center": v(-59.73, -4.93) * mm, "radius": 2.01 * mm});
            skCircle(sketch, "E25.1.3.9", {"center": v(-70.71, -4.35) * mm, "radius": 2.01 * mm});
            skEllipse(sketch, "E25.1.3.10", {"center": v(-60, -2.94) * mm, "majorRadius": 3.02 * mm, "minorRadius": 1.73 * mm, "majorAxis": v(0.58, 0.81)});
            skEllipse(sketch, "E25.1.3.11", {"center": v(-67.71, -9.54) * mm, "majorRadius": 3.02 * mm, "minorRadius": 1.73 * mm, "majorAxis": v(0.16, -0.99)});
            skPoint(sketch, "E25.1.3.12", {"position": v(-65.22, -4.64) * mm});
            skEllipse(sketch, "E25.1.3.13", {"center": v(-62.73, 0.26) * mm, "majorRadius": 3.02 * mm, "minorRadius": 1.73 * mm, "majorAxis": v(-0.16, 0.99)});
            skCircle(sketch, "E25.1.3.14", {"center": v(-69.3, -8.32) * mm, "radius": 2.01 * mm});
            skCircle(sketch, "E25.1.3.15", {"center": v(-61.13, -0.96) * mm, "radius": 2.01 * mm});
            skEllipse(sketch, "E25.1.3.16", {"center": v(-63.52, -9.87) * mm, "majorRadius": 3.02 * mm, "minorRadius": 1.73 * mm, "majorAxis": v(0.81, -0.58)});
            skCircle(sketch, "E25.1.3.17", {"center": v(-65.22, -4.64) * mm, "radius": 5.5 * mm});
            skEllipse(sketch, "E25.1.4.0", {"center": v(-66.92, -24.4) * mm, "majorRadius": 3.02 * mm, "minorRadius": 1.73 * mm, "majorAxis": v(-0.81, 0.58)});
            skCircle(sketch, "E25.1.4.1", {"center": v(-65.51, -35.13) * mm, "radius": 2.01 * mm});
            skCircle(sketch, "E25.1.4.2", {"center": v(-64.93, -24.15) * mm, "radius": 2.01 * mm});
            skCircle(sketch, "E25.1.4.3", {"center": v(-68.9, -25.55) * mm, "radius": 2.01 * mm});
            skEllipse(sketch, "E25.1.4.4", {"center": v(-60.32, -32.13) * mm, "majorRadius": 3.02 * mm, "minorRadius": 1.73 * mm, "majorAxis": v(0.99, 0.16)});
            skEllipse(sketch, "E25.1.4.5", {"center": v(-70.12, -27.15) * mm, "majorRadius": 3.02 * mm, "minorRadius": 1.73 * mm, "majorAxis": v(-0.99, -0.16)});
            skCircle(sketch, "E25.1.4.6", {"center": v(-61.54, -33.73) * mm, "radius": 2.01 * mm});
            skEllipse(sketch, "E25.1.4.7", {"center": v(-70.45, -31.34) * mm, "majorRadius": 3.02 * mm, "minorRadius": 1.73 * mm, "majorAxis": v(-0.58, -0.81)});
            skCircle(sketch, "E25.1.4.8", {"center": v(-59.73, -29.93) * mm, "radius": 2.01 * mm});
            skCircle(sketch, "E25.1.4.9", {"center": v(-70.71, -29.35) * mm, "radius": 2.01 * mm});
            skEllipse(sketch, "E25.1.4.10", {"center": v(-60, -27.94) * mm, "majorRadius": 3.02 * mm, "minorRadius": 1.73 * mm, "majorAxis": v(0.58, 0.81)});
            skEllipse(sketch, "E25.1.4.11", {"center": v(-67.71, -34.54) * mm, "majorRadius": 3.02 * mm, "minorRadius": 1.73 * mm, "majorAxis": v(0.16, -0.99)});
            skPoint(sketch, "E25.1.4.12", {"position": v(-65.22, -29.64) * mm});
            skEllipse(sketch, "E25.1.4.13", {"center": v(-62.73, -24.74) * mm, "majorRadius": 3.02 * mm, "minorRadius": 1.73 * mm, "majorAxis": v(-0.16, 0.99)});
            skCircle(sketch, "E25.1.4.14", {"center": v(-69.3, -33.32) * mm, "radius": 2.01 * mm});
            skCircle(sketch, "E25.1.4.15", {"center": v(-61.13, -25.96) * mm, "radius": 2.01 * mm});
            skEllipse(sketch, "E25.1.4.16", {"center": v(-63.52, -34.87) * mm, "majorRadius": 3.02 * mm, "minorRadius": 1.73 * mm, "majorAxis": v(0.81, -0.58)});
            skCircle(sketch, "E25.1.4.17", {"center": v(-65.22, -29.64) * mm, "radius": 5.5 * mm});
            skEllipse(sketch, "E25.1.5.0", {"center": v(-66.92, -49.4) * mm, "majorRadius": 3.02 * mm, "minorRadius": 1.73 * mm, "majorAxis": v(-0.81, 0.58)});
            skCircle(sketch, "E25.1.5.1", {"center": v(-65.51, -60.13) * mm, "radius": 2.01 * mm});
            skCircle(sketch, "E25.1.5.2", {"center": v(-64.93, -49.15) * mm, "radius": 2.01 * mm});
            skCircle(sketch, "E25.1.5.3", {"center": v(-68.9, -50.55) * mm, "radius": 2.01 * mm});
            skEllipse(sketch, "E25.1.5.4", {"center": v(-60.32, -57.13) * mm, "majorRadius": 3.02 * mm, "minorRadius": 1.73 * mm, "majorAxis": v(0.99, 0.16)});
            skEllipse(sketch, "E25.1.5.5", {"center": v(-70.12, -52.15) * mm, "majorRadius": 3.02 * mm, "minorRadius": 1.73 * mm, "majorAxis": v(-0.99, -0.16)});
            skCircle(sketch, "E25.1.5.6", {"center": v(-61.54, -58.73) * mm, "radius": 2.01 * mm});
            skEllipse(sketch, "E25.1.5.7", {"center": v(-70.45, -56.34) * mm, "majorRadius": 3.02 * mm, "minorRadius": 1.73 * mm, "majorAxis": v(-0.58, -0.81)});
            skCircle(sketch, "E25.1.5.8", {"center": v(-59.73, -54.93) * mm, "radius": 2.01 * mm});
            skCircle(sketch, "E25.1.5.9", {"center": v(-70.71, -54.35) * mm, "radius": 2.01 * mm});
            skEllipse(sketch, "E25.1.5.10", {"center": v(-60, -52.94) * mm, "majorRadius": 3.02 * mm, "minorRadius": 1.73 * mm, "majorAxis": v(0.58, 0.81)});
            skEllipse(sketch, "E25.1.5.11", {"center": v(-67.71, -59.54) * mm, "majorRadius": 3.02 * mm, "minorRadius": 1.73 * mm, "majorAxis": v(0.16, -0.99)});
            skPoint(sketch, "E25.1.5.12", {"position": v(-65.22, -54.64) * mm});
            skEllipse(sketch, "E25.1.5.13", {"center": v(-62.73, -49.74) * mm, "majorRadius": 3.02 * mm, "minorRadius": 1.73 * mm, "majorAxis": v(-0.16, 0.99)});
            skCircle(sketch, "E25.1.5.14", {"center": v(-69.3, -58.32) * mm, "radius": 2.01 * mm});
            skCircle(sketch, "E25.1.5.15", {"center": v(-61.13, -50.96) * mm, "radius": 2.01 * mm});
            skEllipse(sketch, "E25.1.5.16", {"center": v(-63.52, -59.87) * mm, "majorRadius": 3.02 * mm, "minorRadius": 1.73 * mm, "majorAxis": v(0.81, -0.58)});
            skCircle(sketch, "E25.1.5.17", {"center": v(-65.22, -54.64) * mm, "radius": 5.5 * mm});
            skEllipse(sketch, "E25.2.0.0", {"center": v(-40.84, 67.25) * mm, "majorRadius": 3.02 * mm, "minorRadius": 1.73 * mm, "majorAxis": v(-0.81, 0.58)});
            skCircle(sketch, "E25.2.0.1", {"center": v(-39.42, 56.53) * mm, "radius": 2.01 * mm});
            skCircle(sketch, "E25.2.0.2", {"center": v(-38.84, 67.52) * mm, "radius": 2.01 * mm});
            skCircle(sketch, "E25.2.0.3", {"center": v(-42.81, 66.11) * mm, "radius": 2.01 * mm});
            skEllipse(sketch, "E25.2.0.4", {"center": v(-34.23, 59.53) * mm, "majorRadius": 3.02 * mm, "minorRadius": 1.73 * mm, "majorAxis": v(0.99, 0.16)});
            skEllipse(sketch, "E25.2.0.5", {"center": v(-44.03, 64.52) * mm, "majorRadius": 3.02 * mm, "minorRadius": 1.73 * mm, "majorAxis": v(-0.99, -0.16)});
            skCircle(sketch, "E25.2.0.6", {"center": v(-35.45, 57.93) * mm, "radius": 2.01 * mm});
            skEllipse(sketch, "E25.2.0.7", {"center": v(-44.36, 60.32) * mm, "majorRadius": 3.02 * mm, "minorRadius": 1.73 * mm, "majorAxis": v(-0.58, -0.81)});
            skCircle(sketch, "E25.2.0.8", {"center": v(-33.64, 61.73) * mm, "radius": 2.01 * mm});
            skCircle(sketch, "E25.2.0.9", {"center": v(-44.62, 62.31) * mm, "radius": 2.01 * mm});
            skEllipse(sketch, "E25.2.0.10", {"center": v(-33.9, 63.73) * mm, "majorRadius": 3.02 * mm, "minorRadius": 1.73 * mm, "majorAxis": v(0.58, 0.81)});
            skEllipse(sketch, "E25.2.0.11", {"center": v(-41.63, 57.12) * mm, "majorRadius": 3.02 * mm, "minorRadius": 1.73 * mm, "majorAxis": v(0.16, -0.99)});
            skPoint(sketch, "E25.2.0.12", {"position": v(-39.13, 62.02) * mm});
            skEllipse(sketch, "E25.2.0.13", {"center": v(-36.64, 66.93) * mm, "majorRadius": 3.02 * mm, "minorRadius": 1.73 * mm, "majorAxis": v(-0.16, 0.99)});
            skCircle(sketch, "E25.2.0.14", {"center": v(-43.22, 58.35) * mm, "radius": 2.01 * mm});
            skCircle(sketch, "E25.2.0.15", {"center": v(-35.04, 65.7) * mm, "radius": 2.01 * mm});
            skEllipse(sketch, "E25.2.0.16", {"center": v(-37.43, 56.8) * mm, "majorRadius": 3.02 * mm, "minorRadius": 1.73 * mm, "majorAxis": v(0.81, -0.58)});
            skCircle(sketch, "E25.2.0.17", {"center": v(-39.13, 62.02) * mm, "radius": 5.5 * mm});
            skEllipse(sketch, "E25.2.1.0", {"center": v(-40.84, 42.25) * mm, "majorRadius": 3.02 * mm, "minorRadius": 1.73 * mm, "majorAxis": v(-0.81, 0.58)});
            skCircle(sketch, "E25.2.1.1", {"center": v(-39.42, 31.53) * mm, "radius": 2.01 * mm});
            skCircle(sketch, "E25.2.1.2", {"center": v(-38.84, 42.52) * mm, "radius": 2.01 * mm});
            skCircle(sketch, "E25.2.1.3", {"center": v(-42.81, 41.11) * mm, "radius": 2.01 * mm});
            skEllipse(sketch, "E25.2.1.4", {"center": v(-34.23, 34.53) * mm, "majorRadius": 3.02 * mm, "minorRadius": 1.73 * mm, "majorAxis": v(0.99, 0.16)});
            skEllipse(sketch, "E25.2.1.5", {"center": v(-44.03, 39.52) * mm, "majorRadius": 3.02 * mm, "minorRadius": 1.73 * mm, "majorAxis": v(-0.99, -0.16)});
            skCircle(sketch, "E25.2.1.6", {"center": v(-35.45, 32.93) * mm, "radius": 2.01 * mm});
            skEllipse(sketch, "E25.2.1.7", {"center": v(-44.36, 35.32) * mm, "majorRadius": 3.02 * mm, "minorRadius": 1.73 * mm, "majorAxis": v(-0.58, -0.81)});
            skCircle(sketch, "E25.2.1.8", {"center": v(-33.64, 36.73) * mm, "radius": 2.01 * mm});
            skCircle(sketch, "E25.2.1.9", {"center": v(-44.62, 37.31) * mm, "radius": 2.01 * mm});
            skEllipse(sketch, "E25.2.1.10", {"center": v(-33.9, 38.73) * mm, "majorRadius": 3.02 * mm, "minorRadius": 1.73 * mm, "majorAxis": v(0.58, 0.81)});
            skEllipse(sketch, "E25.2.1.11", {"center": v(-41.63, 32.12) * mm, "majorRadius": 3.02 * mm, "minorRadius": 1.73 * mm, "majorAxis": v(0.16, -0.99)});
            skPoint(sketch, "E25.2.1.12", {"position": v(-39.13, 37.02) * mm});
            skEllipse(sketch, "E25.2.1.13", {"center": v(-36.64, 41.93) * mm, "majorRadius": 3.02 * mm, "minorRadius": 1.73 * mm, "majorAxis": v(-0.16, 0.99)});
            skCircle(sketch, "E25.2.1.14", {"center": v(-43.22, 33.35) * mm, "radius": 2.01 * mm});
            skCircle(sketch, "E25.2.1.15", {"center": v(-35.04, 40.7) * mm, "radius": 2.01 * mm});
            skEllipse(sketch, "E25.2.1.16", {"center": v(-37.43, 31.8) * mm, "majorRadius": 3.02 * mm, "minorRadius": 1.73 * mm, "majorAxis": v(0.81, -0.58)});
            skCircle(sketch, "E25.2.1.17", {"center": v(-39.13, 37.02) * mm, "radius": 5.5 * mm});
            skEllipse(sketch, "E25.2.2.0", {"center": v(-40.84, 17.25) * mm, "majorRadius": 3.02 * mm, "minorRadius": 1.73 * mm, "majorAxis": v(-0.81, 0.58)});
            skCircle(sketch, "E25.2.2.1", {"center": v(-39.42, 6.53) * mm, "radius": 2.01 * mm});
            skCircle(sketch, "E25.2.2.2", {"center": v(-38.84, 17.52) * mm, "radius": 2.01 * mm});
            skCircle(sketch, "E25.2.2.3", {"center": v(-42.81, 16.11) * mm, "radius": 2.01 * mm});
            skEllipse(sketch, "E25.2.2.4", {"center": v(-34.23, 9.53) * mm, "majorRadius": 3.02 * mm, "minorRadius": 1.73 * mm, "majorAxis": v(0.99, 0.16)});
            skEllipse(sketch, "E25.2.2.5", {"center": v(-44.03, 14.52) * mm, "majorRadius": 3.02 * mm, "minorRadius": 1.73 * mm, "majorAxis": v(-0.99, -0.16)});
            skCircle(sketch, "E25.2.2.6", {"center": v(-35.45, 7.93) * mm, "radius": 2.01 * mm});
            skEllipse(sketch, "E25.2.2.7", {"center": v(-44.36, 10.32) * mm, "majorRadius": 3.02 * mm, "minorRadius": 1.73 * mm, "majorAxis": v(-0.58, -0.81)});
            skCircle(sketch, "E25.2.2.8", {"center": v(-33.64, 11.73) * mm, "radius": 2.01 * mm});
            skCircle(sketch, "E25.2.2.9", {"center": v(-44.62, 12.31) * mm, "radius": 2.01 * mm});
            skEllipse(sketch, "E25.2.2.10", {"center": v(-33.9, 13.73) * mm, "majorRadius": 3.02 * mm, "minorRadius": 1.73 * mm, "majorAxis": v(0.58, 0.81)});
            skEllipse(sketch, "E25.2.2.11", {"center": v(-41.63, 7.12) * mm, "majorRadius": 3.02 * mm, "minorRadius": 1.73 * mm, "majorAxis": v(0.16, -0.99)});
            skPoint(sketch, "E25.2.2.12", {"position": v(-39.13, 12.02) * mm});
            skEllipse(sketch, "E25.2.2.13", {"center": v(-36.64, 16.93) * mm, "majorRadius": 3.02 * mm, "minorRadius": 1.73 * mm, "majorAxis": v(-0.16, 0.99)});
            skCircle(sketch, "E25.2.2.14", {"center": v(-43.22, 8.35) * mm, "radius": 2.01 * mm});
            skCircle(sketch, "E25.2.2.15", {"center": v(-35.04, 15.7) * mm, "radius": 2.01 * mm});
            skEllipse(sketch, "E25.2.2.16", {"center": v(-37.43, 6.8) * mm, "majorRadius": 3.02 * mm, "minorRadius": 1.73 * mm, "majorAxis": v(0.81, -0.58)});
            skCircle(sketch, "E25.2.2.17", {"center": v(-39.13, 12.02) * mm, "radius": 5.5 * mm});
            skEllipse(sketch, "E25.2.3.0", {"center": v(-40.84, -7.75) * mm, "majorRadius": 3.02 * mm, "minorRadius": 1.73 * mm, "majorAxis": v(-0.81, 0.58)});
            skCircle(sketch, "E25.2.3.1", {"center": v(-39.42, -18.47) * mm, "radius": 2.01 * mm});
            skCircle(sketch, "E25.2.3.2", {"center": v(-38.84, -7.48) * mm, "radius": 2.01 * mm});
            skCircle(sketch, "E25.2.3.3", {"center": v(-42.81, -8.89) * mm, "radius": 2.01 * mm});
            skEllipse(sketch, "E25.2.3.4", {"center": v(-34.23, -15.47) * mm, "majorRadius": 3.02 * mm, "minorRadius": 1.73 * mm, "majorAxis": v(0.99, 0.16)});
            skEllipse(sketch, "E25.2.3.5", {"center": v(-44.03, -10.48) * mm, "majorRadius": 3.02 * mm, "minorRadius": 1.73 * mm, "majorAxis": v(-0.99, -0.16)});
            skCircle(sketch, "E25.2.3.6", {"center": v(-35.45, -17.07) * mm, "radius": 2.01 * mm});
            skEllipse(sketch, "E25.2.3.7", {"center": v(-44.36, -14.68) * mm, "majorRadius": 3.02 * mm, "minorRadius": 1.73 * mm, "majorAxis": v(-0.58, -0.81)});
            skCircle(sketch, "E25.2.3.8", {"center": v(-33.64, -13.27) * mm, "radius": 2.01 * mm});
            skCircle(sketch, "E25.2.3.9", {"center": v(-44.62, -12.69) * mm, "radius": 2.01 * mm});
            skEllipse(sketch, "E25.2.3.10", {"center": v(-33.9, -11.27) * mm, "majorRadius": 3.02 * mm, "minorRadius": 1.73 * mm, "majorAxis": v(0.58, 0.81)});
            skEllipse(sketch, "E25.2.3.11", {"center": v(-41.63, -17.88) * mm, "majorRadius": 3.02 * mm, "minorRadius": 1.73 * mm, "majorAxis": v(0.16, -0.99)});
            skPoint(sketch, "E25.2.3.12", {"position": v(-39.13, -12.98) * mm});
            skEllipse(sketch, "E25.2.3.13", {"center": v(-36.64, -8.07) * mm, "majorRadius": 3.02 * mm, "minorRadius": 1.73 * mm, "majorAxis": v(-0.16, 0.99)});
            skCircle(sketch, "E25.2.3.14", {"center": v(-43.22, -16.65) * mm, "radius": 2.01 * mm});
            skCircle(sketch, "E25.2.3.15", {"center": v(-35.04, -9.3) * mm, "radius": 2.01 * mm});
            skEllipse(sketch, "E25.2.3.16", {"center": v(-37.43, -18.2) * mm, "majorRadius": 3.02 * mm, "minorRadius": 1.73 * mm, "majorAxis": v(0.81, -0.58)});
            skCircle(sketch, "E25.2.3.17", {"center": v(-39.13, -12.98) * mm, "radius": 5.5 * mm});
            skEllipse(sketch, "E25.2.4.0", {"center": v(-40.84, -32.75) * mm, "majorRadius": 3.02 * mm, "minorRadius": 1.73 * mm, "majorAxis": v(-0.81, 0.58)});
            skCircle(sketch, "E25.2.4.1", {"center": v(-39.42, -43.47) * mm, "radius": 2.01 * mm});
            skCircle(sketch, "E25.2.4.2", {"center": v(-38.84, -32.48) * mm, "radius": 2.01 * mm});
            skCircle(sketch, "E25.2.4.3", {"center": v(-42.81, -33.89) * mm, "radius": 2.01 * mm});
            skEllipse(sketch, "E25.2.4.4", {"center": v(-34.23, -40.47) * mm, "majorRadius": 3.02 * mm, "minorRadius": 1.73 * mm, "majorAxis": v(0.99, 0.16)});
            skEllipse(sketch, "E25.2.4.5", {"center": v(-44.03, -35.48) * mm, "majorRadius": 3.02 * mm, "minorRadius": 1.73 * mm, "majorAxis": v(-0.99, -0.16)});
            skCircle(sketch, "E25.2.4.6", {"center": v(-35.45, -42.07) * mm, "radius": 2.01 * mm});
            skEllipse(sketch, "E25.2.4.7", {"center": v(-44.36, -39.68) * mm, "majorRadius": 3.02 * mm, "minorRadius": 1.73 * mm, "majorAxis": v(-0.58, -0.81)});
            skCircle(sketch, "E25.2.4.8", {"center": v(-33.64, -38.27) * mm, "radius": 2.01 * mm});
            skCircle(sketch, "E25.2.4.9", {"center": v(-44.62, -37.69) * mm, "radius": 2.01 * mm});
            skEllipse(sketch, "E25.2.4.10", {"center": v(-33.9, -36.27) * mm, "majorRadius": 3.02 * mm, "minorRadius": 1.73 * mm, "majorAxis": v(0.58, 0.81)});
            skEllipse(sketch, "E25.2.4.11", {"center": v(-41.63, -42.88) * mm, "majorRadius": 3.02 * mm, "minorRadius": 1.73 * mm, "majorAxis": v(0.16, -0.99)});
            skPoint(sketch, "E25.2.4.12", {"position": v(-39.13, -37.98) * mm});
            skEllipse(sketch, "E25.2.4.13", {"center": v(-36.64, -33.07) * mm, "majorRadius": 3.02 * mm, "minorRadius": 1.73 * mm, "majorAxis": v(-0.16, 0.99)});
            skCircle(sketch, "E25.2.4.14", {"center": v(-43.22, -41.65) * mm, "radius": 2.01 * mm});
            skCircle(sketch, "E25.2.4.15", {"center": v(-35.04, -34.3) * mm, "radius": 2.01 * mm});
            skEllipse(sketch, "E25.2.4.16", {"center": v(-37.43, -43.2) * mm, "majorRadius": 3.02 * mm, "minorRadius": 1.73 * mm, "majorAxis": v(0.81, -0.58)});
            skCircle(sketch, "E25.2.4.17", {"center": v(-39.13, -37.98) * mm, "radius": 5.5 * mm});
            skEllipse(sketch, "E25.2.5.0", {"center": v(-40.84, -57.75) * mm, "majorRadius": 3.02 * mm, "minorRadius": 1.73 * mm, "majorAxis": v(-0.81, 0.58)});
            skCircle(sketch, "E25.2.5.1", {"center": v(-39.42, -68.47) * mm, "radius": 2.01 * mm});
            skCircle(sketch, "E25.2.5.2", {"center": v(-38.84, -57.48) * mm, "radius": 2.01 * mm});
            skCircle(sketch, "E25.2.5.3", {"center": v(-42.81, -58.89) * mm, "radius": 2.01 * mm});
            skEllipse(sketch, "E25.2.5.4", {"center": v(-34.23, -65.47) * mm, "majorRadius": 3.02 * mm, "minorRadius": 1.73 * mm, "majorAxis": v(0.99, 0.16)});
            skEllipse(sketch, "E25.2.5.5", {"center": v(-44.03, -60.48) * mm, "majorRadius": 3.02 * mm, "minorRadius": 1.73 * mm, "majorAxis": v(-0.99, -0.16)});
            skCircle(sketch, "E25.2.5.6", {"center": v(-35.45, -67.07) * mm, "radius": 2.01 * mm});
            skEllipse(sketch, "E25.2.5.7", {"center": v(-44.36, -64.68) * mm, "majorRadius": 3.02 * mm, "minorRadius": 1.73 * mm, "majorAxis": v(-0.58, -0.81)});
            skCircle(sketch, "E25.2.5.8", {"center": v(-33.64, -63.27) * mm, "radius": 2.01 * mm});
            skCircle(sketch, "E25.2.5.9", {"center": v(-44.62, -62.69) * mm, "radius": 2.01 * mm});
            skEllipse(sketch, "E25.2.5.10", {"center": v(-33.9, -61.27) * mm, "majorRadius": 3.02 * mm, "minorRadius": 1.73 * mm, "majorAxis": v(0.58, 0.81)});
            skEllipse(sketch, "E25.2.5.11", {"center": v(-41.63, -67.88) * mm, "majorRadius": 3.02 * mm, "minorRadius": 1.73 * mm, "majorAxis": v(0.16, -0.99)});
            skPoint(sketch, "E25.2.5.12", {"position": v(-39.13, -62.98) * mm});
            skEllipse(sketch, "E25.2.5.13", {"center": v(-36.64, -58.07) * mm, "majorRadius": 3.02 * mm, "minorRadius": 1.73 * mm, "majorAxis": v(-0.16, 0.99)});
            skCircle(sketch, "E25.2.5.14", {"center": v(-43.22, -66.65) * mm, "radius": 2.01 * mm});
            skCircle(sketch, "E25.2.5.15", {"center": v(-35.04, -59.3) * mm, "radius": 2.01 * mm});
            skEllipse(sketch, "E25.2.5.16", {"center": v(-37.43, -68.2) * mm, "majorRadius": 3.02 * mm, "minorRadius": 1.73 * mm, "majorAxis": v(0.81, -0.58)});
            skCircle(sketch, "E25.2.5.17", {"center": v(-39.13, -62.98) * mm, "radius": 5.5 * mm});
            skEllipse(sketch, "E25.3.0.0", {"center": v(-14.75, 58.92) * mm, "majorRadius": 3.02 * mm, "minorRadius": 1.73 * mm, "majorAxis": v(-0.81, 0.58)});
            skCircle(sketch, "E25.3.0.1", {"center": v(-13.34, 48.2) * mm, "radius": 2.01 * mm});
            skCircle(sketch, "E25.3.0.2", {"center": v(-12.75, 59.18) * mm, "radius": 2.01 * mm});
            skCircle(sketch, "E25.3.0.3", {"center": v(-16.72, 57.78) * mm, "radius": 2.01 * mm});
            skEllipse(sketch, "E25.3.0.4", {"center": v(-8.14, 51.2) * mm, "majorRadius": 3.02 * mm, "minorRadius": 1.73 * mm, "majorAxis": v(0.99, 0.16)});
            skEllipse(sketch, "E25.3.0.5", {"center": v(-17.95, 56.18) * mm, "majorRadius": 3.02 * mm, "minorRadius": 1.73 * mm, "majorAxis": v(-0.99, -0.16)});
            skCircle(sketch, "E25.3.0.6", {"center": v(-9.37, 49.6) * mm, "radius": 2.01 * mm});
            skEllipse(sketch, "E25.3.0.7", {"center": v(-18.27, 51.98) * mm, "majorRadius": 3.02 * mm, "minorRadius": 1.73 * mm, "majorAxis": v(-0.58, -0.81)});
            skCircle(sketch, "E25.3.0.8", {"center": v(-7.55, 53.4) * mm, "radius": 2.01 * mm});
            skCircle(sketch, "E25.3.0.9", {"center": v(-18.54, 53.98) * mm, "radius": 2.01 * mm});
            skEllipse(sketch, "E25.3.0.10", {"center": v(-7.82, 55.39) * mm, "majorRadius": 3.02 * mm, "minorRadius": 1.73 * mm, "majorAxis": v(0.58, 0.81)});
            skEllipse(sketch, "E25.3.0.11", {"center": v(-15.54, 48.78) * mm, "majorRadius": 3.02 * mm, "minorRadius": 1.73 * mm, "majorAxis": v(0.16, -0.99)});
            skPoint(sketch, "E25.3.0.12", {"position": v(-13.05, 53.69) * mm});
            skEllipse(sketch, "E25.3.0.13", {"center": v(-10.55, 58.59) * mm, "majorRadius": 3.02 * mm, "minorRadius": 1.73 * mm, "majorAxis": v(-0.16, 0.99)});
            skCircle(sketch, "E25.3.0.14", {"center": v(-17.13, 50) * mm, "radius": 2.01 * mm});
            skCircle(sketch, "E25.3.0.15", {"center": v(-8.96, 57.36) * mm, "radius": 2.01 * mm});
            skEllipse(sketch, "E25.3.0.16", {"center": v(-11.34, 48.46) * mm, "majorRadius": 3.02 * mm, "minorRadius": 1.73 * mm, "majorAxis": v(0.81, -0.58)});
            skCircle(sketch, "E25.3.0.17", {"center": v(-13.05, 53.69) * mm, "radius": 5.5 * mm});
            skEllipse(sketch, "E25.3.1.0", {"center": v(-14.75, 33.92) * mm, "majorRadius": 3.02 * mm, "minorRadius": 1.73 * mm, "majorAxis": v(-0.81, 0.58)});
            skCircle(sketch, "E25.3.1.1", {"center": v(-13.34, 23.2) * mm, "radius": 2.01 * mm});
            skCircle(sketch, "E25.3.1.2", {"center": v(-12.75, 34.18) * mm, "radius": 2.01 * mm});
            skCircle(sketch, "E25.3.1.3", {"center": v(-16.72, 32.78) * mm, "radius": 2.01 * mm});
            skEllipse(sketch, "E25.3.1.4", {"center": v(-8.14, 26.2) * mm, "majorRadius": 3.02 * mm, "minorRadius": 1.73 * mm, "majorAxis": v(0.99, 0.16)});
            skEllipse(sketch, "E25.3.1.5", {"center": v(-17.95, 31.18) * mm, "majorRadius": 3.02 * mm, "minorRadius": 1.73 * mm, "majorAxis": v(-0.99, -0.16)});
            skCircle(sketch, "E25.3.1.6", {"center": v(-9.37, 24.6) * mm, "radius": 2.01 * mm});
            skEllipse(sketch, "E25.3.1.7", {"center": v(-18.27, 26.98) * mm, "majorRadius": 3.02 * mm, "minorRadius": 1.73 * mm, "majorAxis": v(-0.58, -0.81)});
            skCircle(sketch, "E25.3.1.8", {"center": v(-7.55, 28.4) * mm, "radius": 2.01 * mm});
            skCircle(sketch, "E25.3.1.9", {"center": v(-18.54, 28.98) * mm, "radius": 2.01 * mm});
            skEllipse(sketch, "E25.3.1.10", {"center": v(-7.82, 30.39) * mm, "majorRadius": 3.02 * mm, "minorRadius": 1.73 * mm, "majorAxis": v(0.58, 0.81)});
            skEllipse(sketch, "E25.3.1.11", {"center": v(-15.54, 23.78) * mm, "majorRadius": 3.02 * mm, "minorRadius": 1.73 * mm, "majorAxis": v(0.16, -0.99)});
            skPoint(sketch, "E25.3.1.12", {"position": v(-13.05, 28.69) * mm});
            skEllipse(sketch, "E25.3.1.13", {"center": v(-10.55, 33.59) * mm, "majorRadius": 3.02 * mm, "minorRadius": 1.73 * mm, "majorAxis": v(-0.16, 0.99)});
            skCircle(sketch, "E25.3.1.14", {"center": v(-17.13, 25) * mm, "radius": 2.01 * mm});
            skCircle(sketch, "E25.3.1.15", {"center": v(-8.96, 32.36) * mm, "radius": 2.01 * mm});
            skEllipse(sketch, "E25.3.1.16", {"center": v(-11.34, 23.46) * mm, "majorRadius": 3.02 * mm, "minorRadius": 1.73 * mm, "majorAxis": v(0.81, -0.58)});
            skCircle(sketch, "E25.3.1.17", {"center": v(-13.05, 28.69) * mm, "radius": 5.5 * mm});
            skEllipse(sketch, "E25.3.2.0", {"center": v(-14.75, 8.92) * mm, "majorRadius": 3.02 * mm, "minorRadius": 1.73 * mm, "majorAxis": v(-0.81, 0.58)});
            skCircle(sketch, "E25.3.2.1", {"center": v(-13.34, -1.8) * mm, "radius": 2.01 * mm});
            skCircle(sketch, "E25.3.2.2", {"center": v(-12.75, 9.18) * mm, "radius": 2.01 * mm});
            skCircle(sketch, "E25.3.2.3", {"center": v(-16.72, 7.78) * mm, "radius": 2.01 * mm});
            skEllipse(sketch, "E25.3.2.4", {"center": v(-8.14, 1.2) * mm, "majorRadius": 3.02 * mm, "minorRadius": 1.73 * mm, "majorAxis": v(0.99, 0.16)});
            skEllipse(sketch, "E25.3.2.5", {"center": v(-17.95, 6.18) * mm, "majorRadius": 3.02 * mm, "minorRadius": 1.73 * mm, "majorAxis": v(-0.99, -0.16)});
            skCircle(sketch, "E25.3.2.6", {"center": v(-9.37, -0.4) * mm, "radius": 2.01 * mm});
            skEllipse(sketch, "E25.3.2.7", {"center": v(-18.27, 1.98) * mm, "majorRadius": 3.02 * mm, "minorRadius": 1.73 * mm, "majorAxis": v(-0.58, -0.81)});
            skCircle(sketch, "E25.3.2.8", {"center": v(-7.55, 3.4) * mm, "radius": 2.01 * mm});
            skCircle(sketch, "E25.3.2.9", {"center": v(-18.54, 3.98) * mm, "radius": 2.01 * mm});
            skEllipse(sketch, "E25.3.2.10", {"center": v(-7.82, 5.39) * mm, "majorRadius": 3.02 * mm, "minorRadius": 1.73 * mm, "majorAxis": v(0.58, 0.81)});
            skEllipse(sketch, "E25.3.2.11", {"center": v(-15.54, -1.22) * mm, "majorRadius": 3.02 * mm, "minorRadius": 1.73 * mm, "majorAxis": v(0.16, -0.99)});
            skPoint(sketch, "E25.3.2.12", {"position": v(-13.05, 3.69) * mm});
            skEllipse(sketch, "E25.3.2.13", {"center": v(-10.55, 8.59) * mm, "majorRadius": 3.02 * mm, "minorRadius": 1.73 * mm, "majorAxis": v(-0.16, 0.99)});
            skCircle(sketch, "E25.3.2.14", {"center": v(-17.13, 0) * mm, "radius": 2.01 * mm});
            skCircle(sketch, "E25.3.2.15", {"center": v(-8.96, 7.36) * mm, "radius": 2.01 * mm});
            skEllipse(sketch, "E25.3.2.16", {"center": v(-11.34, -1.54) * mm, "majorRadius": 3.02 * mm, "minorRadius": 1.73 * mm, "majorAxis": v(0.81, -0.58)});
            skCircle(sketch, "E25.3.2.17", {"center": v(-13.05, 3.69) * mm, "radius": 5.5 * mm});
            skEllipse(sketch, "E25.3.3.0", {"center": v(-14.75, -16.08) * mm, "majorRadius": 3.02 * mm, "minorRadius": 1.73 * mm, "majorAxis": v(-0.81, 0.58)});
            skCircle(sketch, "E25.3.3.1", {"center": v(-13.34, -26.8) * mm, "radius": 2.01 * mm});
            skCircle(sketch, "E25.3.3.2", {"center": v(-12.75, -15.82) * mm, "radius": 2.01 * mm});
            skCircle(sketch, "E25.3.3.3", {"center": v(-16.72, -17.22) * mm, "radius": 2.01 * mm});
            skEllipse(sketch, "E25.3.3.4", {"center": v(-8.14, -23.8) * mm, "majorRadius": 3.02 * mm, "minorRadius": 1.73 * mm, "majorAxis": v(0.99, 0.16)});
            skEllipse(sketch, "E25.3.3.5", {"center": v(-17.95, -18.82) * mm, "majorRadius": 3.02 * mm, "minorRadius": 1.73 * mm, "majorAxis": v(-0.99, -0.16)});
            skCircle(sketch, "E25.3.3.6", {"center": v(-9.37, -25.4) * mm, "radius": 2.01 * mm});
            skEllipse(sketch, "E25.3.3.7", {"center": v(-18.27, -23.02) * mm, "majorRadius": 3.02 * mm, "minorRadius": 1.73 * mm, "majorAxis": v(-0.58, -0.81)});
            skCircle(sketch, "E25.3.3.8", {"center": v(-7.55, -21.6) * mm, "radius": 2.01 * mm});
            skCircle(sketch, "E25.3.3.9", {"center": v(-18.54, -21.02) * mm, "radius": 2.01 * mm});
            skEllipse(sketch, "E25.3.3.10", {"center": v(-7.82, -19.61) * mm, "majorRadius": 3.02 * mm, "minorRadius": 1.73 * mm, "majorAxis": v(0.58, 0.81)});
            skEllipse(sketch, "E25.3.3.11", {"center": v(-15.54, -26.22) * mm, "majorRadius": 3.02 * mm, "minorRadius": 1.73 * mm, "majorAxis": v(0.16, -0.99)});
            skPoint(sketch, "E25.3.3.12", {"position": v(-13.05, -21.31) * mm});
            skEllipse(sketch, "E25.3.3.13", {"center": v(-10.55, -16.41) * mm, "majorRadius": 3.02 * mm, "minorRadius": 1.73 * mm, "majorAxis": v(-0.16, 0.99)});
            skCircle(sketch, "E25.3.3.14", {"center": v(-17.13, -25) * mm, "radius": 2.01 * mm});
            skCircle(sketch, "E25.3.3.15", {"center": v(-8.96, -17.64) * mm, "radius": 2.01 * mm});
            skEllipse(sketch, "E25.3.3.16", {"center": v(-11.34, -26.54) * mm, "majorRadius": 3.02 * mm, "minorRadius": 1.73 * mm, "majorAxis": v(0.81, -0.58)});
            skCircle(sketch, "E25.3.3.17", {"center": v(-13.05, -21.31) * mm, "radius": 5.5 * mm});
            skEllipse(sketch, "E25.3.4.0", {"center": v(-14.75, -41.08) * mm, "majorRadius": 3.02 * mm, "minorRadius": 1.73 * mm, "majorAxis": v(-0.81, 0.58)});
            skCircle(sketch, "E25.3.4.1", {"center": v(-13.34, -51.8) * mm, "radius": 2.01 * mm});
            skCircle(sketch, "E25.3.4.2", {"center": v(-12.75, -40.82) * mm, "radius": 2.01 * mm});
            skCircle(sketch, "E25.3.4.3", {"center": v(-16.72, -42.22) * mm, "radius": 2.01 * mm});
            skEllipse(sketch, "E25.3.4.4", {"center": v(-8.14, -48.8) * mm, "majorRadius": 3.02 * mm, "minorRadius": 1.73 * mm, "majorAxis": v(0.99, 0.16)});
            skEllipse(sketch, "E25.3.4.5", {"center": v(-17.95, -43.82) * mm, "majorRadius": 3.02 * mm, "minorRadius": 1.73 * mm, "majorAxis": v(-0.99, -0.16)});
            skCircle(sketch, "E25.3.4.6", {"center": v(-9.37, -50.4) * mm, "radius": 2.01 * mm});
            skEllipse(sketch, "E25.3.4.7", {"center": v(-18.27, -48.02) * mm, "majorRadius": 3.02 * mm, "minorRadius": 1.73 * mm, "majorAxis": v(-0.58, -0.81)});
            skCircle(sketch, "E25.3.4.8", {"center": v(-7.55, -46.6) * mm, "radius": 2.01 * mm});
            skCircle(sketch, "E25.3.4.9", {"center": v(-18.54, -46.02) * mm, "radius": 2.01 * mm});
            skEllipse(sketch, "E25.3.4.10", {"center": v(-7.82, -44.61) * mm, "majorRadius": 3.02 * mm, "minorRadius": 1.73 * mm, "majorAxis": v(0.58, 0.81)});
            skEllipse(sketch, "E25.3.4.11", {"center": v(-15.54, -51.22) * mm, "majorRadius": 3.02 * mm, "minorRadius": 1.73 * mm, "majorAxis": v(0.16, -0.99)});
            skPoint(sketch, "E25.3.4.12", {"position": v(-13.05, -46.31) * mm});
            skEllipse(sketch, "E25.3.4.13", {"center": v(-10.55, -41.41) * mm, "majorRadius": 3.02 * mm, "minorRadius": 1.73 * mm, "majorAxis": v(-0.16, 0.99)});
            skCircle(sketch, "E25.3.4.14", {"center": v(-17.13, -50) * mm, "radius": 2.01 * mm});
            skCircle(sketch, "E25.3.4.15", {"center": v(-8.96, -42.64) * mm, "radius": 2.01 * mm});
            skEllipse(sketch, "E25.3.4.16", {"center": v(-11.34, -51.54) * mm, "majorRadius": 3.02 * mm, "minorRadius": 1.73 * mm, "majorAxis": v(0.81, -0.58)});
            skCircle(sketch, "E25.3.4.17", {"center": v(-13.05, -46.31) * mm, "radius": 5.5 * mm});
            skEllipse(sketch, "E25.3.5.0", {"center": v(-14.75, -66.08) * mm, "majorRadius": 3.02 * mm, "minorRadius": 1.73 * mm, "majorAxis": v(-0.81, 0.58)});
            skCircle(sketch, "E25.3.5.1", {"center": v(-13.34, -76.8) * mm, "radius": 2.01 * mm});
            skCircle(sketch, "E25.3.5.2", {"center": v(-12.75, -65.82) * mm, "radius": 2.01 * mm});
            skCircle(sketch, "E25.3.5.3", {"center": v(-16.72, -67.22) * mm, "radius": 2.01 * mm});
            skEllipse(sketch, "E25.3.5.4", {"center": v(-8.14, -73.8) * mm, "majorRadius": 3.02 * mm, "minorRadius": 1.73 * mm, "majorAxis": v(0.99, 0.16)});
            skEllipse(sketch, "E25.3.5.5", {"center": v(-17.95, -68.82) * mm, "majorRadius": 3.02 * mm, "minorRadius": 1.73 * mm, "majorAxis": v(-0.99, -0.16)});
            skCircle(sketch, "E25.3.5.6", {"center": v(-9.37, -75.4) * mm, "radius": 2.01 * mm});
            skEllipse(sketch, "E25.3.5.7", {"center": v(-18.27, -73.02) * mm, "majorRadius": 3.02 * mm, "minorRadius": 1.73 * mm, "majorAxis": v(-0.58, -0.81)});
            skCircle(sketch, "E25.3.5.8", {"center": v(-7.55, -71.6) * mm, "radius": 2.01 * mm});
            skCircle(sketch, "E25.3.5.9", {"center": v(-18.54, -71.02) * mm, "radius": 2.01 * mm});
            skEllipse(sketch, "E25.3.5.10", {"center": v(-7.82, -69.61) * mm, "majorRadius": 3.02 * mm, "minorRadius": 1.73 * mm, "majorAxis": v(0.58, 0.81)});
            skEllipse(sketch, "E25.3.5.11", {"center": v(-15.54, -76.22) * mm, "majorRadius": 3.02 * mm, "minorRadius": 1.73 * mm, "majorAxis": v(0.16, -0.99)});
            skPoint(sketch, "E25.3.5.12", {"position": v(-13.05, -71.31) * mm});
            skEllipse(sketch, "E25.3.5.13", {"center": v(-10.55, -66.41) * mm, "majorRadius": 3.02 * mm, "minorRadius": 1.73 * mm, "majorAxis": v(-0.16, 0.99)});
            skCircle(sketch, "E25.3.5.14", {"center": v(-17.13, -75) * mm, "radius": 2.01 * mm});
            skCircle(sketch, "E25.3.5.15", {"center": v(-8.96, -67.64) * mm, "radius": 2.01 * mm});
            skEllipse(sketch, "E25.3.5.16", {"center": v(-11.34, -76.54) * mm, "majorRadius": 3.02 * mm, "minorRadius": 1.73 * mm, "majorAxis": v(0.81, -0.58)});
            skCircle(sketch, "E25.3.5.17", {"center": v(-13.05, -71.31) * mm, "radius": 5.5 * mm});
            skLineSegment(sketch, "E25.direction1", {"start": v(-93.01, 83.93) * mm, "end": v(-66.92, 75.6) * mm, "construction": true});
            skLineSegment(sketch, "E25.direction2", {"start": v(-93.01, 83.93) * mm, "end": v(-93.01, 58.93) * mm, "construction": true});
            skCircle(sketch, "E26.MirrorC", {"center": v(39.13, 62.02) * mm, "radius": 5.5 * mm});
            skEllipse(sketch, "E27.MirrorC", {"center": v(36.64, 66.93) * mm, "majorRadius": 3.02 * mm, "minorRadius": 1.73 * mm, "majorAxis": v(0.16, 0.99)});
            skCircle(sketch, "E28.MirrorC", {"center": v(43.22, 58.35) * mm, "radius": 2.01 * mm});
            skCircle(sketch, "E29.MirrorC", {"center": v(35.04, 65.7) * mm, "radius": 2.01 * mm});
            skEllipse(sketch, "E30.MirrorC", {"center": v(37.43, 56.8) * mm, "majorRadius": 3.02 * mm, "minorRadius": 1.73 * mm, "majorAxis": v(-0.81, -0.58)});
            skEllipse(sketch, "E31.MirrorC", {"center": v(40.84, 67.25) * mm, "majorRadius": 3.02 * mm, "minorRadius": 1.73 * mm, "majorAxis": v(0.81, 0.58)});
            skCircle(sketch, "E32.MirrorC", {"center": v(39.42, 56.53) * mm, "radius": 2.01 * mm});
            skCircle(sketch, "E33.MirrorC", {"center": v(38.84, 67.52) * mm, "radius": 2.01 * mm});
            skCircle(sketch, "E34.MirrorC", {"center": v(42.81, 66.11) * mm, "radius": 2.01 * mm});
            skEllipse(sketch, "E35.MirrorC", {"center": v(34.23, 59.53) * mm, "majorRadius": 3.02 * mm, "minorRadius": 1.73 * mm, "majorAxis": v(-0.99, 0.16)});
            skEllipse(sketch, "E36.MirrorC", {"center": v(44.03, 64.52) * mm, "majorRadius": 3.02 * mm, "minorRadius": 1.73 * mm, "majorAxis": v(0.99, -0.16)});
            skCircle(sketch, "E37.MirrorC", {"center": v(35.45, 57.93) * mm, "radius": 2.01 * mm});
            skEllipse(sketch, "E38.MirrorC", {"center": v(44.36, 60.32) * mm, "majorRadius": 3.02 * mm, "minorRadius": 1.73 * mm, "majorAxis": v(0.58, -0.81)});
            skCircle(sketch, "E39.MirrorC", {"center": v(33.64, 61.73) * mm, "radius": 2.01 * mm});
            skCircle(sketch, "E40.MirrorC", {"center": v(44.62, 62.31) * mm, "radius": 2.01 * mm});
            skEllipse(sketch, "E41.MirrorC", {"center": v(33.9, 63.73) * mm, "majorRadius": 3.02 * mm, "minorRadius": 1.73 * mm, "majorAxis": v(-0.58, 0.81)});
            skEllipse(sketch, "E42.MirrorC", {"center": v(41.63, 57.12) * mm, "majorRadius": 3.02 * mm, "minorRadius": 1.73 * mm, "majorAxis": v(-0.16, -0.99)});
            skEllipse(sketch, "E43.MirrorC", {"center": v(11.34, -76.54) * mm, "majorRadius": 3.02 * mm, "minorRadius": 1.73 * mm, "majorAxis": v(-0.81, -0.58)});
            skEllipse(sketch, "E44.MirrorC", {"center": v(14.75, -41.08) * mm, "majorRadius": 3.02 * mm, "minorRadius": 1.73 * mm, "majorAxis": v(0.81, 0.58)});
            skCircle(sketch, "E45.MirrorC", {"center": v(12.75, 9.18) * mm, "radius": 2.01 * mm});
            skCircle(sketch, "E46.MirrorC", {"center": v(12.75, 34.18) * mm, "radius": 2.01 * mm});
            skCircle(sketch, "E47.MirrorC", {"center": v(13.34, -1.8) * mm, "radius": 2.01 * mm});
            skCircle(sketch, "E48.MirrorC", {"center": v(17.13, -75) * mm, "radius": 2.01 * mm});
            skEllipse(sketch, "E49.MirrorC", {"center": v(11.34, -26.54) * mm, "majorRadius": 3.02 * mm, "minorRadius": 1.73 * mm, "majorAxis": v(-0.81, -0.58)});
            skCircle(sketch, "E50.MirrorC", {"center": v(8.96, 32.36) * mm, "radius": 2.01 * mm});
            skCircle(sketch, "E51.MirrorC", {"center": v(17.13, 25) * mm, "radius": 2.01 * mm});
            skEllipse(sketch, "E52.MirrorC", {"center": v(10.55, 8.59) * mm, "majorRadius": 3.02 * mm, "minorRadius": 1.73 * mm, "majorAxis": v(0.16, 0.99)});
            skEllipse(sketch, "E53.MirrorC", {"center": v(15.54, -26.22) * mm, "majorRadius": 3.02 * mm, "minorRadius": 1.73 * mm, "majorAxis": v(-0.16, -0.99)});
            skCircle(sketch, "E54.MirrorC", {"center": v(8.96, 57.36) * mm, "radius": 2.01 * mm});
            skEllipse(sketch, "E55.MirrorC", {"center": v(10.55, 33.59) * mm, "majorRadius": 3.02 * mm, "minorRadius": 1.73 * mm, "majorAxis": v(0.16, 0.99)});
            skEllipse(sketch, "E56.MirrorC", {"center": v(15.54, 23.78) * mm, "majorRadius": 3.02 * mm, "minorRadius": 1.73 * mm, "majorAxis": v(-0.16, -0.99)});
            skCircle(sketch, "E57.MirrorC", {"center": v(9.37, -75.4) * mm, "radius": 2.01 * mm});
            skEllipse(sketch, "E58.MirrorC", {"center": v(7.82, 55.39) * mm, "majorRadius": 3.02 * mm, "minorRadius": 1.73 * mm, "majorAxis": v(-0.58, 0.81)});
            skEllipse(sketch, "E59.MirrorC", {"center": v(8.14, -73.8) * mm, "majorRadius": 3.02 * mm, "minorRadius": 1.73 * mm, "majorAxis": v(-0.99, 0.16)});
            skCircle(sketch, "E60.MirrorC", {"center": v(7.55, 28.4) * mm, "radius": 2.01 * mm});
            skCircle(sketch, "E61.MirrorC", {"center": v(7.55, 53.4) * mm, "radius": 2.01 * mm});
            skCircle(sketch, "E62.MirrorC", {"center": v(9.37, 24.6) * mm, "radius": 2.01 * mm});
            skCircle(sketch, "E63.MirrorC", {"center": v(16.72, -42.22) * mm, "radius": 2.01 * mm});
            skCircle(sketch, "E64.MirrorC", {"center": v(13.34, -76.8) * mm, "radius": 2.01 * mm});
            skCircle(sketch, "E65.MirrorC", {"center": v(12.75, -40.82) * mm, "radius": 2.01 * mm});
            skCircle(sketch, "E66.MirrorC", {"center": v(13.05, -71.31) * mm, "radius": 5.5 * mm});
            skCircle(sketch, "E67.MirrorC", {"center": v(13.34, -51.8) * mm, "radius": 2.01 * mm});
            skEllipse(sketch, "E68.MirrorC", {"center": v(14.75, -66.08) * mm, "majorRadius": 3.02 * mm, "minorRadius": 1.73 * mm, "majorAxis": v(0.81, 0.58)});
            skEllipse(sketch, "E69.MirrorC", {"center": v(17.95, 56.18) * mm, "majorRadius": 3.02 * mm, "minorRadius": 1.73 * mm, "majorAxis": v(0.99, -0.16)});
            skEllipse(sketch, "E70.MirrorC", {"center": v(8.14, 26.2) * mm, "majorRadius": 3.02 * mm, "minorRadius": 1.73 * mm, "majorAxis": v(-0.99, 0.16)});
            skCircle(sketch, "E71.MirrorC", {"center": v(16.72, 7.78) * mm, "radius": 2.01 * mm});
            skCircle(sketch, "E72.MirrorC", {"center": v(12.75, -15.82) * mm, "radius": 2.01 * mm});
            skCircle(sketch, "E73.MirrorC", {"center": v(13.05, -46.31) * mm, "radius": 5.5 * mm});
            skEllipse(sketch, "E74.MirrorC", {"center": v(8.14, 51.2) * mm, "majorRadius": 3.02 * mm, "minorRadius": 1.73 * mm, "majorAxis": v(-0.99, 0.16)});
            skCircle(sketch, "E75.MirrorC", {"center": v(16.72, 32.78) * mm, "radius": 2.01 * mm});
            skCircle(sketch, "E76.MirrorC", {"center": v(13.34, -26.8) * mm, "radius": 2.01 * mm});
            skCircle(sketch, "E77.MirrorC", {"center": v(8.96, -67.64) * mm, "radius": 2.01 * mm});
            skCircle(sketch, "E78.MirrorC", {"center": v(13.05, -21.31) * mm, "radius": 5.5 * mm});
            skEllipse(sketch, "E79.MirrorC", {"center": v(11.34, -51.54) * mm, "majorRadius": 3.02 * mm, "minorRadius": 1.73 * mm, "majorAxis": v(-0.81, -0.58)});
            skCircle(sketch, "E80.MirrorC", {"center": v(16.72, 57.78) * mm, "radius": 2.01 * mm});
            skEllipse(sketch, "E81.MirrorC", {"center": v(14.75, -16.08) * mm, "majorRadius": 3.02 * mm, "minorRadius": 1.73 * mm, "majorAxis": v(0.81, 0.58)});
            skCircle(sketch, "E82.MirrorC", {"center": v(8.96, -42.64) * mm, "radius": 2.01 * mm});
            skCircle(sketch, "E83.MirrorC", {"center": v(12.75, 59.18) * mm, "radius": 2.01 * mm});
            skCircle(sketch, "E84.MirrorC", {"center": v(13.34, 23.2) * mm, "radius": 2.01 * mm});
            skCircle(sketch, "E85.MirrorC", {"center": v(13.05, 3.69) * mm, "radius": 5.5 * mm});
            skEllipse(sketch, "E86.MirrorC", {"center": v(14.75, 8.92) * mm, "majorRadius": 3.02 * mm, "minorRadius": 1.73 * mm, "majorAxis": v(0.81, 0.58)});
            skEllipse(sketch, "E87.MirrorC", {"center": v(10.55, -66.41) * mm, "majorRadius": 3.02 * mm, "minorRadius": 1.73 * mm, "majorAxis": v(0.16, 0.99)});
            skCircle(sketch, "E88.MirrorC", {"center": v(8.96, -17.64) * mm, "radius": 2.01 * mm});
            skCircle(sketch, "E89.MirrorC", {"center": v(17.13, -50) * mm, "radius": 2.01 * mm});
            skCircle(sketch, "E90.MirrorC", {"center": v(13.34, 48.2) * mm, "radius": 2.01 * mm});
            skEllipse(sketch, "E91.MirrorC", {"center": v(14.75, 33.92) * mm, "majorRadius": 3.02 * mm, "minorRadius": 1.73 * mm, "majorAxis": v(0.81, 0.58)});
            skCircle(sketch, "E92.MirrorC", {"center": v(13.05, 28.69) * mm, "radius": 5.5 * mm});
            skEllipse(sketch, "E93.MirrorC", {"center": v(11.34, -1.54) * mm, "majorRadius": 3.02 * mm, "minorRadius": 1.73 * mm, "majorAxis": v(-0.81, -0.58)});
            skCircle(sketch, "E94.MirrorC", {"center": v(17.13, -25) * mm, "radius": 2.01 * mm});
            skEllipse(sketch, "E95.MirrorC", {"center": v(10.55, -41.41) * mm, "majorRadius": 3.02 * mm, "minorRadius": 1.73 * mm, "majorAxis": v(0.16, 0.99)});
            skEllipse(sketch, "E96.MirrorC", {"center": v(14.75, 58.92) * mm, "majorRadius": 3.02 * mm, "minorRadius": 1.73 * mm, "majorAxis": v(0.81, 0.58)});
            skEllipse(sketch, "E97.MirrorC", {"center": v(11.34, 23.46) * mm, "majorRadius": 3.02 * mm, "minorRadius": 1.73 * mm, "majorAxis": v(-0.81, -0.58)});
            skCircle(sketch, "E98.MirrorC", {"center": v(13.05, 53.69) * mm, "radius": 5.5 * mm});
            skCircle(sketch, "E99.MirrorC", {"center": v(8.96, 7.36) * mm, "radius": 2.01 * mm});
            skEllipse(sketch, "E100.MirrorC", {"center": v(10.55, -16.41) * mm, "majorRadius": 3.02 * mm, "minorRadius": 1.73 * mm, "majorAxis": v(0.16, 0.99)});
            skCircle(sketch, "E101.MirrorC", {"center": v(17.13, 0) * mm, "radius": 2.01 * mm});
            skEllipse(sketch, "E102.MirrorC", {"center": v(15.54, -51.22) * mm, "majorRadius": 3.02 * mm, "minorRadius": 1.73 * mm, "majorAxis": v(-0.16, -0.99)});
            skEllipse(sketch, "E103.MirrorC", {"center": v(11.34, 48.46) * mm, "majorRadius": 3.02 * mm, "minorRadius": 1.73 * mm, "majorAxis": v(-0.81, -0.58)});
            skEllipse(sketch, "E104.MirrorC", {"center": v(7.82, -69.61) * mm, "majorRadius": 3.02 * mm, "minorRadius": 1.73 * mm, "majorAxis": v(-0.58, 0.81)});
            skEllipse(sketch, "E105.MirrorC", {"center": v(7.82, -44.61) * mm, "majorRadius": 3.02 * mm, "minorRadius": 1.73 * mm, "majorAxis": v(-0.58, 0.81)});
            skCircle(sketch, "E106.MirrorC", {"center": v(18.54, -71.02) * mm, "radius": 2.01 * mm});
            skCircle(sketch, "E107.MirrorC", {"center": v(17.13, 50) * mm, "radius": 2.01 * mm});
            skCircle(sketch, "E108.MirrorC", {"center": v(7.55, -71.6) * mm, "radius": 2.01 * mm});
            skEllipse(sketch, "E109.MirrorC", {"center": v(15.54, -1.22) * mm, "majorRadius": 3.02 * mm, "minorRadius": 1.73 * mm, "majorAxis": v(-0.16, -0.99)});
            skEllipse(sketch, "E110.MirrorC", {"center": v(7.82, -19.61) * mm, "majorRadius": 3.02 * mm, "minorRadius": 1.73 * mm, "majorAxis": v(-0.58, 0.81)});
            skCircle(sketch, "E111.MirrorC", {"center": v(18.54, -46.02) * mm, "radius": 2.01 * mm});
            skEllipse(sketch, "E112.MirrorC", {"center": v(18.27, -73.02) * mm, "majorRadius": 3.02 * mm, "minorRadius": 1.73 * mm, "majorAxis": v(0.58, -0.81)});
            skEllipse(sketch, "E113.MirrorC", {"center": v(7.82, 5.39) * mm, "majorRadius": 3.02 * mm, "minorRadius": 1.73 * mm, "majorAxis": v(-0.58, 0.81)});
            skCircle(sketch, "E114.MirrorC", {"center": v(18.54, -21.02) * mm, "radius": 2.01 * mm});
            skCircle(sketch, "E115.MirrorC", {"center": v(7.55, -46.6) * mm, "radius": 2.01 * mm});
            skEllipse(sketch, "E116.MirrorC", {"center": v(10.55, 58.59) * mm, "majorRadius": 3.02 * mm, "minorRadius": 1.73 * mm, "majorAxis": v(0.16, 0.99)});
            skEllipse(sketch, "E117.MirrorC", {"center": v(7.82, 30.39) * mm, "majorRadius": 3.02 * mm, "minorRadius": 1.73 * mm, "majorAxis": v(-0.58, 0.81)});
            skCircle(sketch, "E118.MirrorC", {"center": v(18.54, 3.98) * mm, "radius": 2.01 * mm});
            skCircle(sketch, "E119.MirrorC", {"center": v(7.55, -21.6) * mm, "radius": 2.01 * mm});
            skEllipse(sketch, "E120.MirrorC", {"center": v(18.27, -48.02) * mm, "majorRadius": 3.02 * mm, "minorRadius": 1.73 * mm, "majorAxis": v(0.58, -0.81)});
            skEllipse(sketch, "E121.MirrorC", {"center": v(15.54, 48.78) * mm, "majorRadius": 3.02 * mm, "minorRadius": 1.73 * mm, "majorAxis": v(-0.16, -0.99)});
            skEllipse(sketch, "E122.MirrorC", {"center": v(17.95, -68.82) * mm, "majorRadius": 3.02 * mm, "minorRadius": 1.73 * mm, "majorAxis": v(0.99, -0.16)});
            skCircle(sketch, "E123.MirrorC", {"center": v(18.54, 28.98) * mm, "radius": 2.01 * mm});
            skCircle(sketch, "E124.MirrorC", {"center": v(7.55, 3.4) * mm, "radius": 2.01 * mm});
            skEllipse(sketch, "E125.MirrorC", {"center": v(18.27, -23.02) * mm, "majorRadius": 3.02 * mm, "minorRadius": 1.73 * mm, "majorAxis": v(0.58, -0.81)});
            skCircle(sketch, "E126.MirrorC", {"center": v(9.37, -50.4) * mm, "radius": 2.01 * mm});
            skEllipse(sketch, "E127.MirrorC", {"center": v(18.27, 1.98) * mm, "majorRadius": 3.02 * mm, "minorRadius": 1.73 * mm, "majorAxis": v(0.58, -0.81)});
            skCircle(sketch, "E128.MirrorC", {"center": v(9.37, -25.4) * mm, "radius": 2.01 * mm});
            skEllipse(sketch, "E129.MirrorC", {"center": v(17.95, -43.82) * mm, "majorRadius": 3.02 * mm, "minorRadius": 1.73 * mm, "majorAxis": v(0.99, -0.16)});
            skCircle(sketch, "E130.MirrorC", {"center": v(18.54, 53.98) * mm, "radius": 2.01 * mm});
            skCircle(sketch, "E131.MirrorC", {"center": v(16.72, -67.22) * mm, "radius": 2.01 * mm});
            skEllipse(sketch, "E132.MirrorC", {"center": v(18.27, 26.98) * mm, "majorRadius": 3.02 * mm, "minorRadius": 1.73 * mm, "majorAxis": v(0.58, -0.81)});
            skCircle(sketch, "E133.MirrorC", {"center": v(9.37, -0.4) * mm, "radius": 2.01 * mm});
            skEllipse(sketch, "E134.MirrorC", {"center": v(17.95, -18.82) * mm, "majorRadius": 3.02 * mm, "minorRadius": 1.73 * mm, "majorAxis": v(0.99, -0.16)});
            skEllipse(sketch, "E135.MirrorC", {"center": v(8.14, -48.8) * mm, "majorRadius": 3.02 * mm, "minorRadius": 1.73 * mm, "majorAxis": v(-0.99, 0.16)});
            skEllipse(sketch, "E136.MirrorC", {"center": v(17.95, 6.18) * mm, "majorRadius": 3.02 * mm, "minorRadius": 1.73 * mm, "majorAxis": v(0.99, -0.16)});
            skEllipse(sketch, "E137.MirrorC", {"center": v(8.14, -23.8) * mm, "majorRadius": 3.02 * mm, "minorRadius": 1.73 * mm, "majorAxis": v(-0.99, 0.16)});
            skEllipse(sketch, "E138.MirrorC", {"center": v(18.27, 51.98) * mm, "majorRadius": 3.02 * mm, "minorRadius": 1.73 * mm, "majorAxis": v(0.58, -0.81)});
            skCircle(sketch, "E139.MirrorC", {"center": v(12.75, -65.82) * mm, "radius": 2.01 * mm});
            skCircle(sketch, "E140.MirrorC", {"center": v(9.37, 49.6) * mm, "radius": 2.01 * mm});
            skEllipse(sketch, "E141.MirrorC", {"center": v(17.95, 31.18) * mm, "majorRadius": 3.02 * mm, "minorRadius": 1.73 * mm, "majorAxis": v(0.99, -0.16)});
            skEllipse(sketch, "E142.MirrorC", {"center": v(8.14, 1.2) * mm, "majorRadius": 3.02 * mm, "minorRadius": 1.73 * mm, "majorAxis": v(-0.99, 0.16)});
            skCircle(sketch, "E143.MirrorC", {"center": v(16.72, -17.22) * mm, "radius": 2.01 * mm});
            skCircle(sketch, "E144.MirrorC", {"center": v(65.51, 64.87) * mm, "radius": 2.01 * mm});
            skCircle(sketch, "E145.MirrorC", {"center": v(65.51, 39.87) * mm, "radius": 2.01 * mm});
            skCircle(sketch, "E146.MirrorC", {"center": v(64.93, 75.85) * mm, "radius": 2.01 * mm});
            skCircle(sketch, "E147.MirrorC", {"center": v(61.13, -25.96) * mm, "radius": 2.01 * mm});
            skEllipse(sketch, "E148.MirrorC", {"center": v(63.52, -9.87) * mm, "majorRadius": 3.02 * mm, "minorRadius": 1.73 * mm, "majorAxis": v(-0.81, -0.58)});
            skCircle(sketch, "E149.MirrorC", {"center": v(65.22, 20.36) * mm, "radius": 5.5 * mm});
            skEllipse(sketch, "E150.MirrorC", {"center": v(66.92, 50.6) * mm, "majorRadius": 3.02 * mm, "minorRadius": 1.73 * mm, "majorAxis": v(0.81, 0.58)});
            skCircle(sketch, "E151.MirrorC", {"center": v(69.3, -58.32) * mm, "radius": 2.01 * mm});
            skEllipse(sketch, "E152.MirrorC", {"center": v(41.63, 57.12) * mm, "majorRadius": 3.02 * mm, "minorRadius": 1.73 * mm, "majorAxis": v(-0.16, -0.99)});
            skCircle(sketch, "E153.MirrorC", {"center": v(33.64, -38.27) * mm, "radius": 2.01 * mm});
            skCircle(sketch, "E154.MirrorC", {"center": v(64.93, 50.85) * mm, "radius": 2.01 * mm});
            skCircle(sketch, "E155.MirrorC", {"center": v(68.9, 74.45) * mm, "radius": 2.01 * mm});
            skCircle(sketch, "E156.MirrorC", {"center": v(65.22, -4.64) * mm, "radius": 5.5 * mm});
            skCircle(sketch, "E157.MirrorC", {"center": v(33.64, -63.27) * mm, "radius": 2.01 * mm});
            skCircle(sketch, "E158.MirrorC", {"center": v(44.62, -37.69) * mm, "radius": 2.01 * mm});
            skCircle(sketch, "E159.MirrorC", {"center": v(69.3, -33.32) * mm, "radius": 2.01 * mm});
            skEllipse(sketch, "E160.MirrorC", {"center": v(44.36, -39.68) * mm, "majorRadius": 3.02 * mm, "minorRadius": 1.73 * mm, "majorAxis": v(0.58, -0.81)});
            skCircle(sketch, "E161.MirrorC", {"center": v(68.9, 49.45) * mm, "radius": 2.01 * mm});
            skEllipse(sketch, "E162.MirrorC", {"center": v(60.32, 67.87) * mm, "majorRadius": 3.02 * mm, "minorRadius": 1.73 * mm, "majorAxis": v(-0.99, 0.16)});
            skCircle(sketch, "E163.MirrorC", {"center": v(65.22, -29.64) * mm, "radius": 5.5 * mm});
            skCircle(sketch, "E164.MirrorC", {"center": v(65.51, -10.13) * mm, "radius": 2.01 * mm});
            skEllipse(sketch, "E165.MirrorC", {"center": v(33.9, -36.27) * mm, "majorRadius": 3.02 * mm, "minorRadius": 1.73 * mm, "majorAxis": v(-0.58, 0.81)});
            skEllipse(sketch, "E166.MirrorC", {"center": v(70.12, 72.85) * mm, "majorRadius": 3.02 * mm, "minorRadius": 1.73 * mm, "majorAxis": v(0.99, -0.16)});
            skCircle(sketch, "E167.MirrorC", {"center": v(65.22, -54.64) * mm, "radius": 5.5 * mm});
            skEllipse(sketch, "E168.MirrorC", {"center": v(33.9, -61.27) * mm, "majorRadius": 3.02 * mm, "minorRadius": 1.73 * mm, "majorAxis": v(-0.58, 0.81)});
            skCircle(sketch, "E169.MirrorC", {"center": v(64.93, -24.15) * mm, "radius": 2.01 * mm});
            skEllipse(sketch, "E170.MirrorC", {"center": v(41.63, -67.88) * mm, "majorRadius": 3.02 * mm, "minorRadius": 1.73 * mm, "majorAxis": v(-0.16, -0.99)});
            skEllipse(sketch, "E171.MirrorC", {"center": v(36.64, -58.07) * mm, "majorRadius": 3.02 * mm, "minorRadius": 1.73 * mm, "majorAxis": v(0.16, 0.99)});
            skEllipse(sketch, "E172.MirrorC", {"center": v(60.32, -7.13) * mm, "majorRadius": 3.02 * mm, "minorRadius": 1.73 * mm, "majorAxis": v(-0.99, 0.16)});
            skCircle(sketch, "E173.MirrorC", {"center": v(43.22, -66.65) * mm, "radius": 2.01 * mm});
            skCircle(sketch, "E174.MirrorC", {"center": v(59.73, 70.07) * mm, "radius": 2.01 * mm});
            skEllipse(sketch, "E175.MirrorC", {"center": v(60.32, -32.13) * mm, "majorRadius": 3.02 * mm, "minorRadius": 1.73 * mm, "majorAxis": v(-0.99, 0.16)});
            skEllipse(sketch, "E176.MirrorC", {"center": v(40.84, 17.25) * mm, "majorRadius": 3.02 * mm, "minorRadius": 1.73 * mm, "majorAxis": v(0.81, 0.58)});
            skCircle(sketch, "E177.MirrorC", {"center": v(61.54, -8.73) * mm, "radius": 2.01 * mm});
            skCircle(sketch, "E178.MirrorC", {"center": v(35.04, -59.3) * mm, "radius": 2.01 * mm});
            skEllipse(sketch, "E179.MirrorC", {"center": v(37.43, -43.2) * mm, "majorRadius": 3.02 * mm, "minorRadius": 1.73 * mm, "majorAxis": v(-0.81, -0.58)});
            skEllipse(sketch, "E180.MirrorC", {"center": v(60, 72.06) * mm, "majorRadius": 3.02 * mm, "minorRadius": 1.73 * mm, "majorAxis": v(-0.58, 0.81)});
            skEllipse(sketch, "E181.MirrorC", {"center": v(70.45, -6.34) * mm, "majorRadius": 3.02 * mm, "minorRadius": 1.73 * mm, "majorAxis": v(0.58, -0.81)});
            skEllipse(sketch, "E182.MirrorC", {"center": v(70.45, -31.34) * mm, "majorRadius": 3.02 * mm, "minorRadius": 1.73 * mm, "majorAxis": v(0.58, -0.81)});
            skCircle(sketch, "E183.MirrorC", {"center": v(59.73, -4.93) * mm, "radius": 2.01 * mm});
            skCircle(sketch, "E184.MirrorC", {"center": v(42.81, 16.11) * mm, "radius": 2.01 * mm});
            skCircle(sketch, "E185.MirrorC", {"center": v(39.13, -62.98) * mm, "radius": 5.5 * mm});
            skEllipse(sketch, "E186.MirrorC", {"center": v(70.45, -56.34) * mm, "majorRadius": 3.02 * mm, "minorRadius": 1.73 * mm, "majorAxis": v(0.58, -0.81)});
            skCircle(sketch, "E187.MirrorC", {"center": v(59.73, -29.93) * mm, "radius": 2.01 * mm});
            skCircle(sketch, "E188.MirrorC", {"center": v(39.42, -68.47) * mm, "radius": 2.01 * mm});
            skCircle(sketch, "E189.MirrorC", {"center": v(38.84, -57.48) * mm, "radius": 2.01 * mm});
            skCircle(sketch, "E190.MirrorC", {"center": v(70.71, -54.35) * mm, "radius": 2.01 * mm});
            skCircle(sketch, "E191.MirrorC", {"center": v(35.45, -42.07) * mm, "radius": 2.01 * mm});
            skEllipse(sketch, "E192.MirrorC", {"center": v(62.73, -24.74) * mm, "majorRadius": 3.02 * mm, "minorRadius": 1.73 * mm, "majorAxis": v(0.16, 0.99)});
            skEllipse(sketch, "E193.MirrorC", {"center": v(67.71, -34.54) * mm, "majorRadius": 3.02 * mm, "minorRadius": 1.73 * mm, "majorAxis": v(-0.16, -0.99)});
            skEllipse(sketch, "E194.MirrorC", {"center": v(66.92, 75.6) * mm, "majorRadius": 3.02 * mm, "minorRadius": 1.73 * mm, "majorAxis": v(0.81, 0.58)});
            skEllipse(sketch, "E195.MirrorC", {"center": v(63.52, 65.13) * mm, "majorRadius": 3.02 * mm, "minorRadius": 1.73 * mm, "majorAxis": v(-0.81, -0.58)});
            skCircle(sketch, "E196.MirrorC", {"center": v(61.13, -0.96) * mm, "radius": 2.01 * mm});
            skEllipse(sketch, "E197.MirrorC", {"center": v(63.52, 15.13) * mm, "majorRadius": 3.02 * mm, "minorRadius": 1.73 * mm, "majorAxis": v(-0.81, -0.58)});
            skCircle(sketch, "E198.MirrorC", {"center": v(65.22, 45.36) * mm, "radius": 5.5 * mm});
            skEllipse(sketch, "E199.MirrorC", {"center": v(66.92, 25.6) * mm, "majorRadius": 3.02 * mm, "minorRadius": 1.73 * mm, "majorAxis": v(0.81, 0.58)});
            skEllipse(sketch, "E200.MirrorC", {"center": v(33.9, 13.73) * mm, "majorRadius": 3.02 * mm, "minorRadius": 1.73 * mm, "majorAxis": v(-0.58, 0.81)});
            skEllipse(sketch, "E201.MirrorC", {"center": v(33.9, 38.73) * mm, "majorRadius": 3.02 * mm, "minorRadius": 1.73 * mm, "majorAxis": v(-0.58, 0.81)});
            skEllipse(sketch, "E202.MirrorC", {"center": v(41.63, 32.12) * mm, "majorRadius": 3.02 * mm, "minorRadius": 1.73 * mm, "majorAxis": v(-0.16, -0.99)});
            skEllipse(sketch, "E203.MirrorC", {"center": v(36.64, 66.93) * mm, "majorRadius": 3.02 * mm, "minorRadius": 1.73 * mm, "majorAxis": v(0.16, 0.99)});
            skEllipse(sketch, "E204.MirrorC", {"center": v(44.36, -64.68) * mm, "majorRadius": 3.02 * mm, "minorRadius": 1.73 * mm, "majorAxis": v(0.58, -0.81)});
            skCircle(sketch, "E205.MirrorC", {"center": v(44.62, -12.69) * mm, "radius": 2.01 * mm});
            skEllipse(sketch, "E206.MirrorC", {"center": v(62.73, -49.74) * mm, "majorRadius": 3.02 * mm, "minorRadius": 1.73 * mm, "majorAxis": v(0.16, 0.99)});
            skEllipse(sketch, "E207.MirrorC", {"center": v(63.52, -34.87) * mm, "majorRadius": 3.02 * mm, "minorRadius": 1.73 * mm, "majorAxis": v(-0.81, -0.58)});
            skEllipse(sketch, "E208.MirrorC", {"center": v(66.92, 0.6) * mm, "majorRadius": 3.02 * mm, "minorRadius": 1.73 * mm, "majorAxis": v(0.81, 0.58)});
            skCircle(sketch, "E209.MirrorC", {"center": v(65.51, 14.87) * mm, "radius": 2.01 * mm});
            skEllipse(sketch, "E210.MirrorC", {"center": v(41.63, 7.12) * mm, "majorRadius": 3.02 * mm, "minorRadius": 1.73 * mm, "majorAxis": v(-0.16, -0.99)});
            skEllipse(sketch, "E211.MirrorC", {"center": v(36.64, 41.93) * mm, "majorRadius": 3.02 * mm, "minorRadius": 1.73 * mm, "majorAxis": v(0.16, 0.99)});
            skCircle(sketch, "E212.MirrorC", {"center": v(61.13, -50.96) * mm, "radius": 2.01 * mm});
            skEllipse(sketch, "E213.MirrorC", {"center": v(33.9, -11.27) * mm, "majorRadius": 3.02 * mm, "minorRadius": 1.73 * mm, "majorAxis": v(-0.58, 0.81)});
            skCircle(sketch, "E214.MirrorC", {"center": v(35.45, -67.07) * mm, "radius": 2.01 * mm});
            skCircle(sketch, "E215.MirrorC", {"center": v(44.62, 12.31) * mm, "radius": 2.01 * mm});
            skCircle(sketch, "E216.MirrorC", {"center": v(33.64, -13.27) * mm, "radius": 2.01 * mm});
            skEllipse(sketch, "E217.MirrorC", {"center": v(66.92, -24.4) * mm, "majorRadius": 3.02 * mm, "minorRadius": 1.73 * mm, "majorAxis": v(0.81, 0.58)});
            skEllipse(sketch, "E218.MirrorC", {"center": v(36.64, 16.93) * mm, "majorRadius": 3.02 * mm, "minorRadius": 1.73 * mm, "majorAxis": v(0.16, 0.99)});
            skCircle(sketch, "E219.MirrorC", {"center": v(64.93, 25.85) * mm, "radius": 2.01 * mm});
            skCircle(sketch, "E220.MirrorC", {"center": v(43.22, 33.35) * mm, "radius": 2.01 * mm});
            skEllipse(sketch, "E221.MirrorC", {"center": v(63.52, -59.87) * mm, "majorRadius": 3.02 * mm, "minorRadius": 1.73 * mm, "majorAxis": v(-0.81, -0.58)});
            skCircle(sketch, "E222.MirrorC", {"center": v(44.62, -62.69) * mm, "radius": 2.01 * mm});
            skEllipse(sketch, "E223.MirrorC", {"center": v(41.63, -17.88) * mm, "majorRadius": 3.02 * mm, "minorRadius": 1.73 * mm, "majorAxis": v(-0.16, -0.99)});
            skEllipse(sketch, "E224.MirrorC", {"center": v(60.32, 42.87) * mm, "majorRadius": 3.02 * mm, "minorRadius": 1.73 * mm, "majorAxis": v(-0.99, 0.16)});
            skEllipse(sketch, "E225.MirrorC", {"center": v(66.92, -49.4) * mm, "majorRadius": 3.02 * mm, "minorRadius": 1.73 * mm, "majorAxis": v(0.81, 0.58)});
            skCircle(sketch, "E226.MirrorC", {"center": v(65.51, -35.13) * mm, "radius": 2.01 * mm});
            skCircle(sketch, "E227.MirrorC", {"center": v(64.93, 0.85) * mm, "radius": 2.01 * mm});
            skCircle(sketch, "E228.MirrorC", {"center": v(68.9, 24.45) * mm, "radius": 2.01 * mm});
            skCircle(sketch, "E229.MirrorC", {"center": v(43.22, 8.35) * mm, "radius": 2.01 * mm});
            skCircle(sketch, "E230.MirrorC", {"center": v(35.04, 40.7) * mm, "radius": 2.01 * mm});
            skEllipse(sketch, "E231.MirrorC", {"center": v(37.43, 56.8) * mm, "majorRadius": 3.02 * mm, "minorRadius": 1.73 * mm, "majorAxis": v(-0.81, -0.58)});
            skEllipse(sketch, "E232.MirrorC", {"center": v(41.63, -42.88) * mm, "majorRadius": 3.02 * mm, "minorRadius": 1.73 * mm, "majorAxis": v(-0.16, -0.99)});
            skEllipse(sketch, "E233.MirrorC", {"center": v(36.64, -8.07) * mm, "majorRadius": 3.02 * mm, "minorRadius": 1.73 * mm, "majorAxis": v(0.16, 0.99)});
            skCircle(sketch, "E234.MirrorC", {"center": v(65.51, -60.13) * mm, "radius": 2.01 * mm});
            skCircle(sketch, "E235.MirrorC", {"center": v(68.9, -0.55) * mm, "radius": 2.01 * mm});
            skEllipse(sketch, "E236.MirrorC", {"center": v(60.32, 17.87) * mm, "majorRadius": 3.02 * mm, "minorRadius": 1.73 * mm, "majorAxis": v(-0.99, 0.16)});
            skCircle(sketch, "E237.MirrorC", {"center": v(35.04, 15.7) * mm, "radius": 2.01 * mm});
            skEllipse(sketch, "E238.MirrorC", {"center": v(37.43, 31.8) * mm, "majorRadius": 3.02 * mm, "minorRadius": 1.73 * mm, "majorAxis": v(-0.81, -0.58)});
            skEllipse(sketch, "E239.MirrorC", {"center": v(40.84, 67.25) * mm, "majorRadius": 3.02 * mm, "minorRadius": 1.73 * mm, "majorAxis": v(0.81, 0.58)});
            skEllipse(sketch, "E240.MirrorC", {"center": v(36.64, -33.07) * mm, "majorRadius": 3.02 * mm, "minorRadius": 1.73 * mm, "majorAxis": v(0.16, 0.99)});
            skCircle(sketch, "E241.MirrorC", {"center": v(43.22, -16.65) * mm, "radius": 2.01 * mm});
            skEllipse(sketch, "E242.MirrorC", {"center": v(70.12, 47.85) * mm, "majorRadius": 3.02 * mm, "minorRadius": 1.73 * mm, "majorAxis": v(0.99, -0.16)});
            skCircle(sketch, "E243.MirrorC", {"center": v(61.54, 66.27) * mm, "radius": 2.01 * mm});
            skEllipse(sketch, "E244.MirrorC", {"center": v(37.43, 6.8) * mm, "majorRadius": 3.02 * mm, "minorRadius": 1.73 * mm, "majorAxis": v(-0.81, -0.58)});
            skCircle(sketch, "E245.MirrorC", {"center": v(39.13, 37.02) * mm, "radius": 5.5 * mm});
            skEllipse(sketch, "E246.MirrorC", {"center": v(40.84, 42.25) * mm, "majorRadius": 3.02 * mm, "minorRadius": 1.73 * mm, "majorAxis": v(0.81, 0.58)});
            skCircle(sketch, "E247.MirrorC", {"center": v(43.22, -41.65) * mm, "radius": 2.01 * mm});
            skCircle(sketch, "E248.MirrorC", {"center": v(35.04, -9.3) * mm, "radius": 2.01 * mm});
            skCircle(sketch, "E249.MirrorC", {"center": v(61.54, 41.27) * mm, "radius": 2.01 * mm});
            skEllipse(sketch, "E250.MirrorC", {"center": v(70.45, 68.66) * mm, "majorRadius": 3.02 * mm, "minorRadius": 1.73 * mm, "majorAxis": v(0.58, -0.81)});
            skCircle(sketch, "E251.MirrorC", {"center": v(64.93, -49.15) * mm, "radius": 2.01 * mm});
            skCircle(sketch, "E252.MirrorC", {"center": v(68.9, -25.55) * mm, "radius": 2.01 * mm});
            skEllipse(sketch, "E253.MirrorC", {"center": v(70.12, 22.85) * mm, "majorRadius": 3.02 * mm, "minorRadius": 1.73 * mm, "majorAxis": v(0.99, -0.16)});
            skEllipse(sketch, "E254.MirrorC", {"center": v(37.43, -18.2) * mm, "majorRadius": 3.02 * mm, "minorRadius": 1.73 * mm, "majorAxis": v(-0.81, -0.58)});
            skCircle(sketch, "E255.MirrorC", {"center": v(35.04, -34.3) * mm, "radius": 2.01 * mm});
            skEllipse(sketch, "E256.MirrorC", {"center": v(70.45, 43.66) * mm, "majorRadius": 3.02 * mm, "minorRadius": 1.73 * mm, "majorAxis": v(0.58, -0.81)});
            skCircle(sketch, "E257.MirrorC", {"center": v(68.9, -50.55) * mm, "radius": 2.01 * mm});
            skEllipse(sketch, "E258.MirrorC", {"center": v(70.12, -2.15) * mm, "majorRadius": 3.02 * mm, "minorRadius": 1.73 * mm, "majorAxis": v(0.99, -0.16)});
            skCircle(sketch, "E259.MirrorC", {"center": v(61.54, 16.27) * mm, "radius": 2.01 * mm});
            skCircle(sketch, "E260.MirrorC", {"center": v(39.13, 12.02) * mm, "radius": 5.5 * mm});
            skCircle(sketch, "E261.MirrorC", {"center": v(39.42, 31.53) * mm, "radius": 2.01 * mm});
            skCircle(sketch, "E262.MirrorC", {"center": v(59.73, 45.07) * mm, "radius": 2.01 * mm});
            skCircle(sketch, "E263.MirrorC", {"center": v(70.71, 70.65) * mm, "radius": 2.01 * mm});
            skEllipse(sketch, "E264.MirrorC", {"center": v(60.32, -57.13) * mm, "majorRadius": 3.02 * mm, "minorRadius": 1.73 * mm, "majorAxis": v(-0.99, 0.16)});
            skEllipse(sketch, "E265.MirrorC", {"center": v(70.12, -27.15) * mm, "majorRadius": 3.02 * mm, "minorRadius": 1.73 * mm, "majorAxis": v(0.99, -0.16)});
            skEllipse(sketch, "E266.MirrorC", {"center": v(70.45, 18.66) * mm, "majorRadius": 3.02 * mm, "minorRadius": 1.73 * mm, "majorAxis": v(0.58, -0.81)});
            skEllipse(sketch, "E267.MirrorC", {"center": v(40.84, -7.75) * mm, "majorRadius": 3.02 * mm, "minorRadius": 1.73 * mm, "majorAxis": v(0.81, 0.58)});
            skCircle(sketch, "E268.MirrorC", {"center": v(39.42, 6.53) * mm, "radius": 2.01 * mm});
            skCircle(sketch, "E269.MirrorC", {"center": v(38.84, 42.52) * mm, "radius": 2.01 * mm});
            skCircle(sketch, "E270.MirrorC", {"center": v(39.13, -12.98) * mm, "radius": 5.5 * mm});
            skCircle(sketch, "E271.MirrorC", {"center": v(70.71, 45.65) * mm, "radius": 2.01 * mm});
            skEllipse(sketch, "E272.MirrorC", {"center": v(70.12, -52.15) * mm, "majorRadius": 3.02 * mm, "minorRadius": 1.73 * mm, "majorAxis": v(0.99, -0.16)});
            skCircle(sketch, "E273.MirrorC", {"center": v(61.54, -33.73) * mm, "radius": 2.01 * mm});
            skCircle(sketch, "E274.MirrorC", {"center": v(59.73, 20.07) * mm, "radius": 2.01 * mm});
            skCircle(sketch, "E275.MirrorC", {"center": v(38.84, 17.52) * mm, "radius": 2.01 * mm});
            skCircle(sketch, "E276.MirrorC", {"center": v(39.42, -18.47) * mm, "radius": 2.01 * mm});
            skCircle(sketch, "E277.MirrorC", {"center": v(42.81, 41.11) * mm, "radius": 2.01 * mm});
            skEllipse(sketch, "E278.MirrorC", {"center": v(34.23, 59.53) * mm, "majorRadius": 3.02 * mm, "minorRadius": 1.73 * mm, "majorAxis": v(-0.99, 0.16)});
            skEllipse(sketch, "E279.MirrorC", {"center": v(37.43, -68.2) * mm, "majorRadius": 3.02 * mm, "minorRadius": 1.73 * mm, "majorAxis": v(-0.81, -0.58)});
            skCircle(sketch, "E280.MirrorC", {"center": v(39.13, -37.98) * mm, "radius": 5.5 * mm});
            skEllipse(sketch, "E281.MirrorC", {"center": v(40.84, -32.75) * mm, "majorRadius": 3.02 * mm, "minorRadius": 1.73 * mm, "majorAxis": v(0.81, 0.58)});
            skEllipse(sketch, "E282.MirrorC", {"center": v(60, 47.06) * mm, "majorRadius": 3.02 * mm, "minorRadius": 1.73 * mm, "majorAxis": v(-0.58, 0.81)});
            skEllipse(sketch, "E283.MirrorC", {"center": v(67.71, 65.46) * mm, "majorRadius": 3.02 * mm, "minorRadius": 1.73 * mm, "majorAxis": v(-0.16, -0.99)});
            skCircle(sketch, "E284.MirrorC", {"center": v(61.54, -58.73) * mm, "radius": 2.01 * mm});
            skCircle(sketch, "E285.MirrorC", {"center": v(70.71, 20.65) * mm, "radius": 2.01 * mm});
            skCircle(sketch, "E286.MirrorC", {"center": v(38.84, -7.48) * mm, "radius": 2.01 * mm});
            skEllipse(sketch, "E287.MirrorC", {"center": v(34.23, 34.53) * mm, "majorRadius": 3.02 * mm, "minorRadius": 1.73 * mm, "majorAxis": v(-0.99, 0.16)});
            skEllipse(sketch, "E288.MirrorC", {"center": v(44.03, 64.52) * mm, "majorRadius": 3.02 * mm, "minorRadius": 1.73 * mm, "majorAxis": v(0.99, -0.16)});
            skEllipse(sketch, "E289.MirrorC", {"center": v(40.84, -57.75) * mm, "majorRadius": 3.02 * mm, "minorRadius": 1.73 * mm, "majorAxis": v(0.81, 0.58)});
            skCircle(sketch, "E290.MirrorC", {"center": v(39.42, -43.47) * mm, "radius": 2.01 * mm});
            skCircle(sketch, "E291.MirrorC", {"center": v(70.71, -4.35) * mm, "radius": 2.01 * mm});
            skEllipse(sketch, "E292.MirrorC", {"center": v(60, 22.06) * mm, "majorRadius": 3.02 * mm, "minorRadius": 1.73 * mm, "majorAxis": v(-0.58, 0.81)});
            skEllipse(sketch, "E293.MirrorC", {"center": v(67.71, 40.46) * mm, "majorRadius": 3.02 * mm, "minorRadius": 1.73 * mm, "majorAxis": v(-0.16, -0.99)});
            skEllipse(sketch, "E294.MirrorC", {"center": v(62.73, 75.26) * mm, "majorRadius": 3.02 * mm, "minorRadius": 1.73 * mm, "majorAxis": v(0.16, 0.99)});
            skEllipse(sketch, "E295.MirrorC", {"center": v(44.03, 39.52) * mm, "majorRadius": 3.02 * mm, "minorRadius": 1.73 * mm, "majorAxis": v(0.99, -0.16)});
            skCircle(sketch, "E296.MirrorC", {"center": v(38.84, -32.48) * mm, "radius": 2.01 * mm});
            skCircle(sketch, "E297.MirrorC", {"center": v(42.81, -8.89) * mm, "radius": 2.01 * mm});
            skEllipse(sketch, "E298.MirrorC", {"center": v(34.23, 9.53) * mm, "majorRadius": 3.02 * mm, "minorRadius": 1.73 * mm, "majorAxis": v(-0.99, 0.16)});
            skEllipse(sketch, "E299.MirrorC", {"center": v(60, -2.94) * mm, "majorRadius": 3.02 * mm, "minorRadius": 1.73 * mm, "majorAxis": v(-0.58, 0.81)});
            skEllipse(sketch, "E300.MirrorC", {"center": v(67.71, 15.46) * mm, "majorRadius": 3.02 * mm, "minorRadius": 1.73 * mm, "majorAxis": v(-0.16, -0.99)});
            skEllipse(sketch, "E301.MirrorC", {"center": v(62.73, 50.26) * mm, "majorRadius": 3.02 * mm, "minorRadius": 1.73 * mm, "majorAxis": v(0.16, 0.99)});
            skCircle(sketch, "E302.MirrorC", {"center": v(69.3, 66.68) * mm, "radius": 2.01 * mm});
            skCircle(sketch, "E303.MirrorC", {"center": v(35.45, 32.93) * mm, "radius": 2.01 * mm});
            skEllipse(sketch, "E304.MirrorC", {"center": v(44.36, 60.32) * mm, "majorRadius": 3.02 * mm, "minorRadius": 1.73 * mm, "majorAxis": v(0.58, -0.81)});
            skCircle(sketch, "E305.MirrorC", {"center": v(59.73, -54.93) * mm, "radius": 2.01 * mm});
            skCircle(sketch, "E306.MirrorC", {"center": v(70.71, -29.35) * mm, "radius": 2.01 * mm});
            skCircle(sketch, "E307.MirrorC", {"center": v(42.81, -33.89) * mm, "radius": 2.01 * mm});
            skEllipse(sketch, "E308.MirrorC", {"center": v(34.23, -15.47) * mm, "majorRadius": 3.02 * mm, "minorRadius": 1.73 * mm, "majorAxis": v(-0.99, 0.16)});
            skEllipse(sketch, "E309.MirrorC", {"center": v(44.03, 14.52) * mm, "majorRadius": 3.02 * mm, "minorRadius": 1.73 * mm, "majorAxis": v(0.99, -0.16)});
            skEllipse(sketch, "E310.MirrorC", {"center": v(67.71, -9.54) * mm, "majorRadius": 3.02 * mm, "minorRadius": 1.73 * mm, "majorAxis": v(-0.16, -0.99)});
            skEllipse(sketch, "E311.MirrorC", {"center": v(62.73, 25.26) * mm, "majorRadius": 3.02 * mm, "minorRadius": 1.73 * mm, "majorAxis": v(0.16, 0.99)});
            skCircle(sketch, "E312.MirrorC", {"center": v(69.3, 41.68) * mm, "radius": 2.01 * mm});
            skCircle(sketch, "E313.MirrorC", {"center": v(61.13, 74.04) * mm, "radius": 2.01 * mm});
            skEllipse(sketch, "E314.MirrorC", {"center": v(44.36, 35.32) * mm, "majorRadius": 3.02 * mm, "minorRadius": 1.73 * mm, "majorAxis": v(0.58, -0.81)});
            skEllipse(sketch, "E315.MirrorC", {"center": v(60, -27.94) * mm, "majorRadius": 3.02 * mm, "minorRadius": 1.73 * mm, "majorAxis": v(-0.58, 0.81)});
            skCircle(sketch, "E316.MirrorC", {"center": v(33.64, 11.73) * mm, "radius": 2.01 * mm});
            skEllipse(sketch, "E317.MirrorC", {"center": v(44.36, -14.68) * mm, "majorRadius": 3.02 * mm, "minorRadius": 1.73 * mm, "majorAxis": v(0.58, -0.81)});
            skEllipse(sketch, "E318.MirrorC", {"center": v(44.03, -60.48) * mm, "majorRadius": 3.02 * mm, "minorRadius": 1.73 * mm, "majorAxis": v(0.99, -0.16)});
            skEllipse(sketch, "E319.MirrorC", {"center": v(67.71, -59.54) * mm, "majorRadius": 3.02 * mm, "minorRadius": 1.73 * mm, "majorAxis": v(-0.16, -0.99)});
            skEllipse(sketch, "E320.MirrorC", {"center": v(33.9, 63.73) * mm, "majorRadius": 3.02 * mm, "minorRadius": 1.73 * mm, "majorAxis": v(-0.58, 0.81)});
            skCircle(sketch, "E321.MirrorC", {"center": v(65.22, 70.36) * mm, "radius": 5.5 * mm});
            skCircle(sketch, "E322.MirrorC", {"center": v(44.62, 37.31) * mm, "radius": 2.01 * mm});
            skEllipse(sketch, "E323.MirrorC", {"center": v(63.52, 40.13) * mm, "majorRadius": 3.02 * mm, "minorRadius": 1.73 * mm, "majorAxis": v(-0.81, -0.58)});
            skCircle(sketch, "E324.MirrorC", {"center": v(61.13, 24.04) * mm, "radius": 2.01 * mm});
            skCircle(sketch, "E325.MirrorC", {"center": v(69.3, -8.32) * mm, "radius": 2.01 * mm});
            skEllipse(sketch, "E326.MirrorC", {"center": v(44.36, 10.32) * mm, "majorRadius": 3.02 * mm, "minorRadius": 1.73 * mm, "majorAxis": v(0.58, -0.81)});
            skCircle(sketch, "E327.MirrorC", {"center": v(35.45, -17.07) * mm, "radius": 2.01 * mm});
            skEllipse(sketch, "E328.MirrorC", {"center": v(44.03, -35.48) * mm, "majorRadius": 3.02 * mm, "minorRadius": 1.73 * mm, "majorAxis": v(0.99, -0.16)});
            skEllipse(sketch, "E329.MirrorC", {"center": v(34.23, -65.47) * mm, "majorRadius": 3.02 * mm, "minorRadius": 1.73 * mm, "majorAxis": v(-0.99, 0.16)});
            skEllipse(sketch, "E330.MirrorC", {"center": v(60, -52.94) * mm, "majorRadius": 3.02 * mm, "minorRadius": 1.73 * mm, "majorAxis": v(-0.58, 0.81)});
            skCircle(sketch, "E331.MirrorC", {"center": v(69.3, 16.68) * mm, "radius": 2.01 * mm});
            skCircle(sketch, "E332.MirrorC", {"center": v(61.13, 49.04) * mm, "radius": 2.01 * mm});
            skEllipse(sketch, "E333.MirrorC", {"center": v(62.73, 0.26) * mm, "majorRadius": 3.02 * mm, "minorRadius": 1.73 * mm, "majorAxis": v(0.16, 0.99)});
            skCircle(sketch, "E334.MirrorC", {"center": v(35.45, 7.93) * mm, "radius": 2.01 * mm});
            skEllipse(sketch, "E335.MirrorC", {"center": v(44.03, -10.48) * mm, "majorRadius": 3.02 * mm, "minorRadius": 1.73 * mm, "majorAxis": v(0.99, -0.16)});
            skEllipse(sketch, "E336.MirrorC", {"center": v(34.23, -40.47) * mm, "majorRadius": 3.02 * mm, "minorRadius": 1.73 * mm, "majorAxis": v(-0.99, 0.16)});
            skCircle(sketch, "E337.MirrorC", {"center": v(42.81, -58.89) * mm, "radius": 2.01 * mm});
            skCircle(sketch, "E338.MirrorC", {"center": v(33.64, 36.73) * mm, "radius": 2.01 * mm});
            skEllipse(sketch, "E339.MirrorC", {"center": v(60.32, 67.87) * mm, "majorRadius": 3.02 * mm, "minorRadius": 1.73 * mm, "majorAxis": v(-0.99, 0.16)});
            skEllipse(sketch, "E340.MirrorC", {"center": v(70.12, 72.85) * mm, "majorRadius": 3.02 * mm, "minorRadius": 1.73 * mm, "majorAxis": v(0.99, -0.16)});
            skEllipse(sketch, "E341.MirrorC", {"center": v(70.45, 68.66) * mm, "majorRadius": 3.02 * mm, "minorRadius": 1.73 * mm, "majorAxis": v(0.58, -0.81)});
            skEllipse(sketch, "E342.MirrorC", {"center": v(66.92, 75.6) * mm, "majorRadius": 3.02 * mm, "minorRadius": 1.73 * mm, "majorAxis": v(0.81, 0.58)});
            skEllipse(sketch, "E343.MirrorC", {"center": v(63.52, 65.13) * mm, "majorRadius": 3.02 * mm, "minorRadius": 1.73 * mm, "majorAxis": v(-0.81, -0.58)});
            skEllipse(sketch, "E344.MirrorC", {"center": v(62.73, 75.26) * mm, "majorRadius": 3.02 * mm, "minorRadius": 1.73 * mm, "majorAxis": v(0.16, 0.99)});
            skEllipse(sketch, "E345.MirrorC", {"center": v(67.71, 65.46) * mm, "majorRadius": 3.02 * mm, "minorRadius": 1.73 * mm, "majorAxis": v(-0.16, -0.99)});
            skEllipse(sketch, "E346.MirrorC", {"center": v(60, 72.06) * mm, "majorRadius": 3.02 * mm, "minorRadius": 1.73 * mm, "majorAxis": v(-0.58, 0.81)});
            skArc(sketch, "E347.MirrorCS", {"start": v(96.52, 88.35) * mm, "mid": v(98.75, 87.66) * mm, "end": v(100.56, 86.17) * mm});
            skCircle(sketch, "E348.MirrorC", {"center": v(94.99, 82.79) * mm, "radius": 2.01 * mm});
            skCircle(sketch, "E349.MirrorC", {"center": v(91.02, 84.2) * mm, "radius": 2.01 * mm});
            skEllipse(sketch, "E350.MirrorC", {"center": v(93.01, 83.93) * mm, "majorRadius": 3.02 * mm, "minorRadius": 1.73 * mm, "majorAxis": v(0.81, 0.58)});
            skCircle(sketch, "E351.MirrorC", {"center": v(87.63, 24.6) * mm, "radius": 2.01 * mm});
            skEllipse(sketch, "E352.MirrorC", {"center": v(96.54, 52) * mm, "majorRadius": 3.02 * mm, "minorRadius": 1.73 * mm, "majorAxis": v(0.58, -0.81)});
            skCircle(sketch, "E353.MirrorC", {"center": v(87.63, -0.4) * mm, "radius": 2.01 * mm});
            skCircle(sketch, "E354.MirrorC", {"center": v(85.82, 53.4) * mm, "radius": 2.01 * mm});
            skCircle(sketch, "E355.MirrorC", {"center": v(85.82, 28.4) * mm, "radius": 2.01 * mm});
            skCircle(sketch, "E356.MirrorC", {"center": v(96.8, 53.99) * mm, "radius": 2.01 * mm});
            skCircle(sketch, "E357.MirrorC", {"center": v(85.82, 3.4) * mm, "radius": 2.01 * mm});
            skEllipse(sketch, "E358.MirrorC", {"center": v(93.8, 23.8) * mm, "majorRadius": 3.02 * mm, "minorRadius": 1.73 * mm, "majorAxis": v(-0.16, -0.99)});
            skEllipse(sketch, "E359.MirrorC", {"center": v(96.2, 81.2) * mm, "majorRadius": 3.02 * mm, "minorRadius": 1.73 * mm, "majorAxis": v(0.99, -0.16)});
            skCircle(sketch, "E360.MirrorC", {"center": v(91.02, -15.8) * mm, "radius": 2.01 * mm});
            skCircle(sketch, "E361.MirrorC", {"center": v(91.6, -26.8) * mm, "radius": 2.01 * mm});
            skEllipse(sketch, "E362.MirrorC", {"center": v(86.4, 51.2) * mm, "majorRadius": 3.02 * mm, "minorRadius": 1.73 * mm, "majorAxis": v(-0.99, 0.16)});
            skEllipse(sketch, "E363.MirrorC", {"center": v(93.01, -16.07) * mm, "majorRadius": 3.02 * mm, "minorRadius": 1.73 * mm, "majorAxis": v(0.81, 0.58)});
            skEllipse(sketch, "E364.MirrorC", {"center": v(89.6, -51.53) * mm, "majorRadius": 3.02 * mm, "minorRadius": 1.73 * mm, "majorAxis": v(-0.81, -0.58)});
            skCircle(sketch, "E365.MirrorC", {"center": v(87.22, 82.38) * mm, "radius": 2.01 * mm});
            skEllipse(sketch, "E366.MirrorC", {"center": v(88.81, 83.6) * mm, "majorRadius": 3.02 * mm, "minorRadius": 1.73 * mm, "majorAxis": v(0.16, 0.99)});
            skCircle(sketch, "E367.MirrorC", {"center": v(91.02, 59.2) * mm, "radius": 2.01 * mm});
            skCircle(sketch, "E368.MirrorC", {"center": v(91.6, 48.2) * mm, "radius": 2.01 * mm});
            skEllipse(sketch, "E369.MirrorC", {"center": v(93.8, 48.8) * mm, "majorRadius": 3.02 * mm, "minorRadius": 1.73 * mm, "majorAxis": v(-0.16, -0.99)});
            skEllipse(sketch, "E370.MirrorC", {"center": v(93.01, 58.93) * mm, "majorRadius": 3.02 * mm, "minorRadius": 1.73 * mm, "majorAxis": v(0.81, 0.58)});
            skEllipse(sketch, "E371.MirrorC", {"center": v(88.81, -16.4) * mm, "majorRadius": 3.02 * mm, "minorRadius": 1.73 * mm, "majorAxis": v(0.16, 0.99)});
            skEllipse(sketch, "E372.MirrorC", {"center": v(93.8, -51.2) * mm, "majorRadius": 3.02 * mm, "minorRadius": 1.73 * mm, "majorAxis": v(-0.16, -0.99)});
            skEllipse(sketch, "E373.MirrorC", {"center": v(89.6, 48.47) * mm, "majorRadius": 3.02 * mm, "minorRadius": 1.73 * mm, "majorAxis": v(-0.81, -0.58)});
            skCircle(sketch, "E374.MirrorC", {"center": v(95.4, 50.02) * mm, "radius": 2.01 * mm});
            skCircle(sketch, "E375.MirrorC", {"center": v(95.4, 25.02) * mm, "radius": 2.01 * mm});
            skLineSegment(sketch, "E376.MirrorCS", {"start": v(93.01, 83.93) * mm, "end": v(66.92, 75.6) * mm, "construction": true});
            skEllipse(sketch, "E377.MirrorC", {"center": v(96.2, 6.2) * mm, "majorRadius": 3.02 * mm, "minorRadius": 1.73 * mm, "majorAxis": v(0.99, -0.16)});
            skCircle(sketch, "E378.MirrorC", {"center": v(94.99, -42.21) * mm, "radius": 2.01 * mm});
            skEllipse(sketch, "E379.MirrorC", {"center": v(86.4, -23.8) * mm, "majorRadius": 3.02 * mm, "minorRadius": 1.73 * mm, "majorAxis": v(-0.99, 0.16)});
            skEllipse(sketch, "E380.MirrorC", {"center": v(96.54, 27) * mm, "majorRadius": 3.02 * mm, "minorRadius": 1.73 * mm, "majorAxis": v(0.58, -0.81)});
            skEllipse(sketch, "E381.MirrorC", {"center": v(96.54, 77) * mm, "majorRadius": 3.02 * mm, "minorRadius": 1.73 * mm, "majorAxis": v(0.58, -0.81)});
            skEllipse(sketch, "E382.MirrorC", {"center": v(86.4, -48.8) * mm, "majorRadius": 3.02 * mm, "minorRadius": 1.73 * mm, "majorAxis": v(-0.99, 0.16)});
            skEllipse(sketch, "E383.MirrorC", {"center": v(96.2, -18.8) * mm, "majorRadius": 3.02 * mm, "minorRadius": 1.73 * mm, "majorAxis": v(0.99, -0.16)});
            skEllipse(sketch, "E384.MirrorC", {"center": v(96.54, 2) * mm, "majorRadius": 3.02 * mm, "minorRadius": 1.73 * mm, "majorAxis": v(0.58, -0.81)});
            skCircle(sketch, "E385.MirrorC", {"center": v(96.8, 78.99) * mm, "radius": 2.01 * mm});
            skEllipse(sketch, "E386.MirrorC", {"center": v(96.2, -43.8) * mm, "majorRadius": 3.02 * mm, "minorRadius": 1.73 * mm, "majorAxis": v(0.99, -0.16)});
            skCircle(sketch, "E387.MirrorC", {"center": v(87.63, -25.4) * mm, "radius": 2.01 * mm});
            skCircle(sketch, "E388.MirrorC", {"center": v(87.63, -50.4) * mm, "radius": 2.01 * mm});
            skEllipse(sketch, "E389.MirrorC", {"center": v(96.54, -23) * mm, "majorRadius": 3.02 * mm, "minorRadius": 1.73 * mm, "majorAxis": v(0.58, -0.81)});
            skCircle(sketch, "E390.MirrorC", {"center": v(96.8, 28.99) * mm, "radius": 2.01 * mm});
            skEllipse(sketch, "E391.MirrorC", {"center": v(86.08, 55.4) * mm, "majorRadius": 3.02 * mm, "minorRadius": 1.73 * mm, "majorAxis": v(-0.58, 0.81)});
            skEllipse(sketch, "E392.MirrorC", {"center": v(93.8, 73.8) * mm, "majorRadius": 3.02 * mm, "minorRadius": 1.73 * mm, "majorAxis": v(-0.16, -0.99)});
            skCircle(sketch, "E393.MirrorC", {"center": v(96.8, -21.01) * mm, "radius": 2.01 * mm});
            skCircle(sketch, "E394.MirrorC", {"center": v(85.82, -46.6) * mm, "radius": 2.01 * mm});
            skEllipse(sketch, "E395.MirrorC", {"center": v(89.6, 73.47) * mm, "majorRadius": 3.02 * mm, "minorRadius": 1.73 * mm, "majorAxis": v(-0.81, -0.58)});
            skEllipse(sketch, "E396.MirrorC", {"center": v(88.81, 58.6) * mm, "majorRadius": 3.02 * mm, "minorRadius": 1.73 * mm, "majorAxis": v(0.16, 0.99)});
            skEllipse(sketch, "E397.MirrorC", {"center": v(86.08, 5.4) * mm, "majorRadius": 3.02 * mm, "minorRadius": 1.73 * mm, "majorAxis": v(-0.58, 0.81)});
            skEllipse(sketch, "E398.MirrorC", {"center": v(86.4, 1.2) * mm, "majorRadius": 3.02 * mm, "minorRadius": 1.73 * mm, "majorAxis": v(-0.99, 0.16)});
            skCircle(sketch, "E399.MirrorC", {"center": v(94.99, -17.21) * mm, "radius": 2.01 * mm});
            skCircle(sketch, "E400.MirrorC", {"center": v(91.02, -40.8) * mm, "radius": 2.01 * mm});
            skCircle(sketch, "E401.MirrorC", {"center": v(87.63, 49.6) * mm, "radius": 2.01 * mm});
            skEllipse(sketch, "E402.MirrorC", {"center": v(96.2, 31.2) * mm, "majorRadius": 3.02 * mm, "minorRadius": 1.73 * mm, "majorAxis": v(0.99, -0.16)});
            skCircle(sketch, "E403.MirrorC", {"center": v(94.99, 7.79) * mm, "radius": 2.01 * mm});
            skCircle(sketch, "E404.MirrorC", {"center": v(91.6, -51.8) * mm, "radius": 2.01 * mm});
            skEllipse(sketch, "E405.MirrorC", {"center": v(96.2, 56.2) * mm, "majorRadius": 3.02 * mm, "minorRadius": 1.73 * mm, "majorAxis": v(0.99, -0.16)});
            skEllipse(sketch, "E406.MirrorC", {"center": v(86.4, 26.2) * mm, "majorRadius": 3.02 * mm, "minorRadius": 1.73 * mm, "majorAxis": v(-0.99, 0.16)});
            skCircle(sketch, "E407.MirrorC", {"center": v(91.02, 9.2) * mm, "radius": 2.01 * mm});
            skEllipse(sketch, "E408.MirrorC", {"center": v(93.01, -41.07) * mm, "majorRadius": 3.02 * mm, "minorRadius": 1.73 * mm, "majorAxis": v(0.81, 0.58)});
            skCircle(sketch, "E409.MirrorC", {"center": v(91.3, -46.3) * mm, "radius": 5.5 * mm});
            skCircle(sketch, "E410.MirrorC", {"center": v(94.99, 32.79) * mm, "radius": 2.01 * mm});
            skCircle(sketch, "E411.MirrorC", {"center": v(91.6, -1.8) * mm, "radius": 2.01 * mm});
            skCircle(sketch, "E412.MirrorC", {"center": v(91.3, -21.3) * mm, "radius": 5.5 * mm});
            skCircle(sketch, "E413.MirrorC", {"center": v(94.99, 57.79) * mm, "radius": 2.01 * mm});
            skCircle(sketch, "E414.MirrorC", {"center": v(91.02, 34.2) * mm, "radius": 2.01 * mm});
            skEllipse(sketch, "E415.MirrorC", {"center": v(93.01, 8.93) * mm, "majorRadius": 3.02 * mm, "minorRadius": 1.73 * mm, "majorAxis": v(0.81, 0.58)});
            skCircle(sketch, "E416.MirrorC", {"center": v(91.3, 3.7) * mm, "radius": 5.5 * mm});
            skEllipse(sketch, "E417.MirrorC", {"center": v(89.6, -26.53) * mm, "majorRadius": 3.02 * mm, "minorRadius": 1.73 * mm, "majorAxis": v(-0.81, -0.58)});
            skCircle(sketch, "E418.MirrorC", {"center": v(87.22, -42.62) * mm, "radius": 2.01 * mm});
            skCircle(sketch, "E419.MirrorC", {"center": v(91.6, 23.2) * mm, "radius": 2.01 * mm});
            skCircle(sketch, "E420.MirrorC", {"center": v(91.3, 28.7) * mm, "radius": 5.5 * mm});
            skEllipse(sketch, "E421.MirrorC", {"center": v(89.6, -1.53) * mm, "majorRadius": 3.02 * mm, "minorRadius": 1.73 * mm, "majorAxis": v(-0.81, -0.58)});
            skCircle(sketch, "E422.MirrorC", {"center": v(87.22, -17.62) * mm, "radius": 2.01 * mm});
            skCircle(sketch, "E423.MirrorC", {"center": v(95.4, -49.98) * mm, "radius": 2.01 * mm});
            skEllipse(sketch, "E424.MirrorC", {"center": v(86.08, 80.4) * mm, "majorRadius": 3.02 * mm, "minorRadius": 1.73 * mm, "majorAxis": v(-0.58, 0.81)});
            skEllipse(sketch, "E425.MirrorC", {"center": v(93.01, 33.93) * mm, "majorRadius": 3.02 * mm, "minorRadius": 1.73 * mm, "majorAxis": v(0.81, 0.58)});
            skCircle(sketch, "E426.MirrorC", {"center": v(85.82, -21.6) * mm, "radius": 2.01 * mm});
            skEllipse(sketch, "E427.MirrorC", {"center": v(96.54, -48) * mm, "majorRadius": 3.02 * mm, "minorRadius": 1.73 * mm, "majorAxis": v(0.58, -0.81)});
            skCircle(sketch, "E428.MirrorC", {"center": v(95.4, 75.02) * mm, "radius": 2.01 * mm});
            skEllipse(sketch, "E429.MirrorC", {"center": v(86.08, 30.4) * mm, "majorRadius": 3.02 * mm, "minorRadius": 1.73 * mm, "majorAxis": v(-0.58, 0.81)});
            skCircle(sketch, "E430.MirrorC", {"center": v(96.8, 3.99) * mm, "radius": 2.01 * mm});
            skCircle(sketch, "E431.MirrorC", {"center": v(95.4, -24.98) * mm, "radius": 2.01 * mm});
            skEllipse(sketch, "E432.MirrorC", {"center": v(88.81, -41.4) * mm, "majorRadius": 3.02 * mm, "minorRadius": 1.73 * mm, "majorAxis": v(0.16, 0.99)});
            skCircle(sketch, "E433.MirrorC", {"center": v(91.3, 53.7) * mm, "radius": 5.5 * mm});
            skEllipse(sketch, "E434.MirrorC", {"center": v(89.6, 23.47) * mm, "majorRadius": 3.02 * mm, "minorRadius": 1.73 * mm, "majorAxis": v(-0.81, -0.58)});
            skCircle(sketch, "E435.MirrorC", {"center": v(87.22, 7.38) * mm, "radius": 2.01 * mm});
            skCircle(sketch, "E436.MirrorC", {"center": v(85.82, 78.4) * mm, "radius": 2.01 * mm});
            skCircle(sketch, "E437.MirrorC", {"center": v(87.63, 74.6) * mm, "radius": 2.01 * mm});
            skCircle(sketch, "E438.MirrorC", {"center": v(87.22, 32.38) * mm, "radius": 2.01 * mm});
            skCircle(sketch, "E439.MirrorC", {"center": v(95.4, 0.02) * mm, "radius": 2.01 * mm});
            skCircle(sketch, "E440.MirrorC", {"center": v(91.3, 78.7) * mm, "radius": 5.5 * mm});
            skEllipse(sketch, "E441.MirrorC", {"center": v(93.8, -1.2) * mm, "majorRadius": 3.02 * mm, "minorRadius": 1.73 * mm, "majorAxis": v(-0.16, -0.99)});
            skEllipse(sketch, "E442.MirrorC", {"center": v(88.81, 33.6) * mm, "majorRadius": 3.02 * mm, "minorRadius": 1.73 * mm, "majorAxis": v(0.16, 0.99)});
            skCircle(sketch, "E443.MirrorC", {"center": v(91.6, 73.2) * mm, "radius": 2.01 * mm});
            skCircle(sketch, "E444.MirrorC", {"center": v(96.8, -46.01) * mm, "radius": 2.01 * mm});
            skEllipse(sketch, "E445.MirrorC", {"center": v(86.08, -19.6) * mm, "majorRadius": 3.02 * mm, "minorRadius": 1.73 * mm, "majorAxis": v(-0.58, 0.81)});
            skEllipse(sketch, "E446.MirrorC", {"center": v(88.81, 8.6) * mm, "majorRadius": 3.02 * mm, "minorRadius": 1.73 * mm, "majorAxis": v(0.16, 0.99)});
            skEllipse(sketch, "E447.MirrorC", {"center": v(86.4, 76.2) * mm, "majorRadius": 3.02 * mm, "minorRadius": 1.73 * mm, "majorAxis": v(-0.99, 0.16)});
            skEllipse(sketch, "E448.MirrorC", {"center": v(93.8, -26.2) * mm, "majorRadius": 3.02 * mm, "minorRadius": 1.73 * mm, "majorAxis": v(-0.16, -0.99)});
            skEllipse(sketch, "E449.MirrorC", {"center": v(86.08, -44.6) * mm, "majorRadius": 3.02 * mm, "minorRadius": 1.73 * mm, "majorAxis": v(-0.58, 0.81)});
            skCircle(sketch, "E450.MirrorC", {"center": v(87.22, 57.38) * mm, "radius": 2.01 * mm});
            skLineSegment(sketch, "E451.MirrorCS", {"start": v(93.01, 83.93) * mm, "end": v(93.01, 58.93) * mm, "construction": true});
            skLineSegment(sketch, "E452.MirrorCS", {"start": v(116.5, 0) * mm, "end": v(-139.03, 0) * mm, "construction": true});
            skSolve(sketch);
        }
        {
            var Q0;
            Q0=makeQuery(id+"F0.imprint","IMPRINT",FACE,{"disambiguationData":[TD([[makeQuery(id+"F0.imprint","IMPRINT",EDGE,{"derivedFrom":sQuery(id+"F0.wireOp",EDGE,"E8")}),1.0]])]});
            extrude(context, id + "F1", {"entities" : qUnion([Q0]), "depth" : 1.5 * mm});
        }
        {
            var Q0;
            Q0=makeQuery(id+"F0.imprint","IMPRINT",FACE,{"disambiguationData":[TD([[makeQuery(id+"F0.imprint","IMPRINT",EDGE,{"derivedFrom":sQuery(id+"F0.wireOp",EDGE,"E14.0")}),1.0]])]});
            extrude(context, id + "F2", {"entities" : qUnion([Q0]), "operationType" : NewBodyOperationType.ADD, "depth" : 1 * mm});
        }
    });
